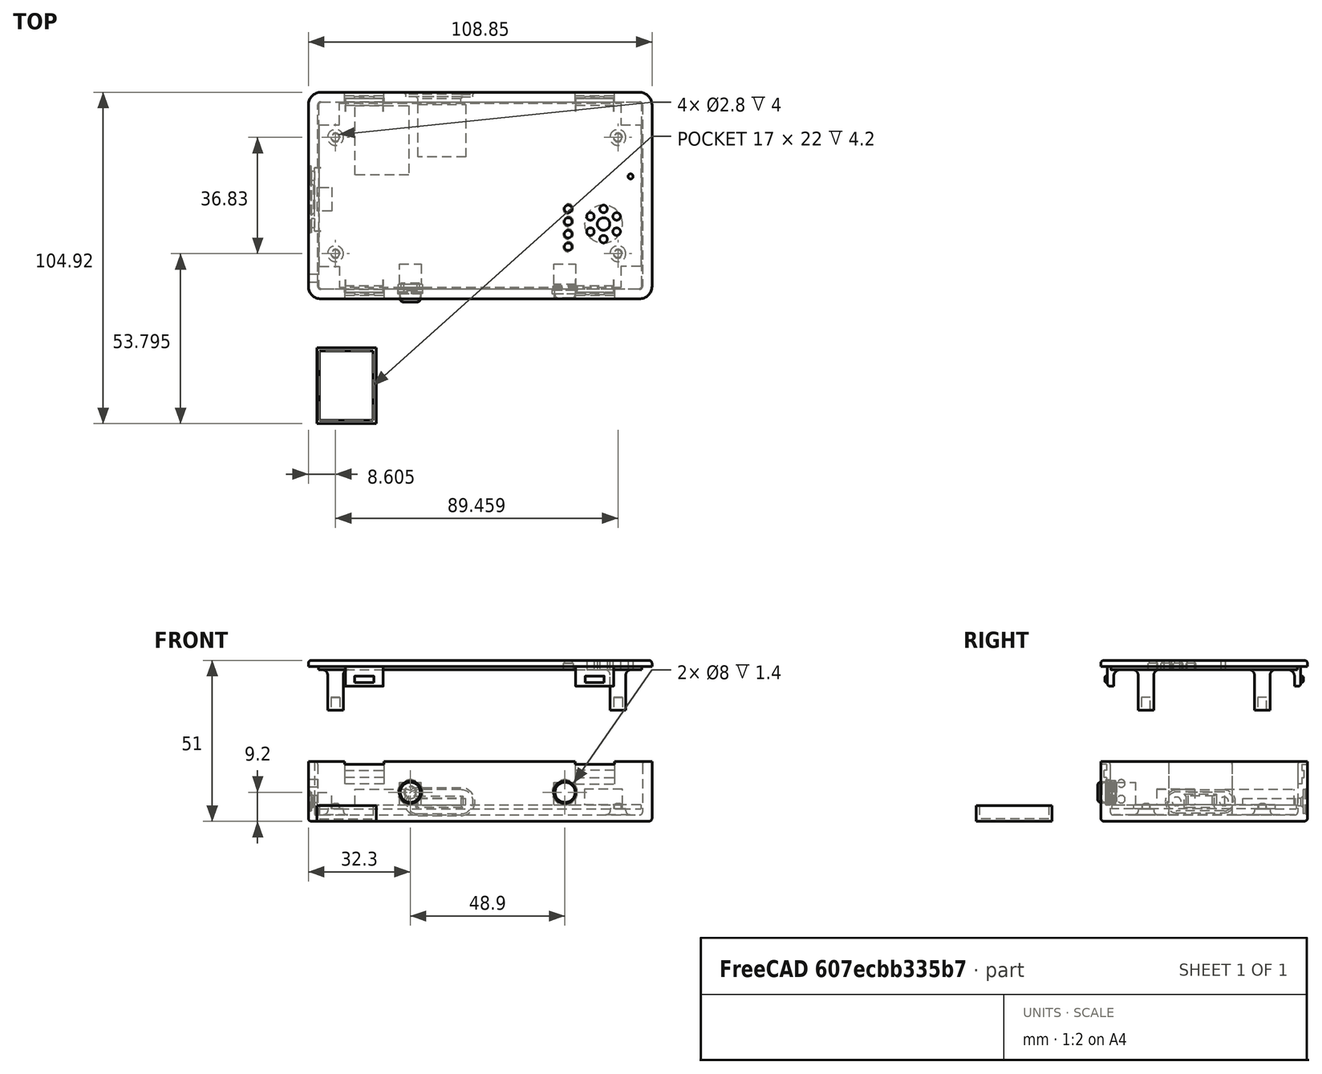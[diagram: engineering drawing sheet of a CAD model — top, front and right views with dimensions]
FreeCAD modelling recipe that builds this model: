
FCSTD DOCUMENT  (FreeCAD 0.17R13541 (Git))
Label: Variometer-Case-Rev2
License: All rights reserved
LicenseURL: http://en.wikipedia.org/wiki/All_rights_reserved
objects: Sketcher::SketchObject×48, PartDesign::Pad×24, PartDesign::Pocket×20, PartDesign::Fillet×18, PartDesign::Plane×12, PartDesign::Body×9, Mesh::Feature×5, PartDesign::ShapeBinder×4, PartDesign::Chamfer×3, Part::Feature×2
note: 184 computed .brp shape members not serialized (recipe doc carries the construction recipe); baked Part::Feature solids carry a one-line shape summary decoded from their .brp

FEATURE [Sketcher::SketchObject] Sketch  label="MasterSketch"
  MapMode = 5
  Support = -> [XY_Plane]
  sketch-geometry (27):
    g0: LineSegment StartX=0 StartY=58.42 StartZ=0 EndX=101.85 EndY=58.42 EndZ=0
    g1: LineSegment StartX=101.85 StartY=58.42 StartZ=0 EndX=101.85 EndY=0 EndZ=0
    g2: LineSegment StartX=101.85 StartY=0 StartZ=0 EndX=0 EndY=0 EndZ=0
    g3: LineSegment StartX=0 StartY=0 StartZ=0 EndX=0 EndY=58.42 EndZ=0
    g4: Circle CenterX=5.105 CenterY=10.795 CenterZ=0 NormalX=0 NormalY=0 NormalZ=1 AngleXU=0 Radius=2.5
    g5: Circle CenterX=5.105 CenterY=47.625 CenterZ=0 NormalX=0 NormalY=0 NormalZ=1 AngleXU=0 Radius=2.5
    g6: Circle CenterX=94.564 CenterY=10.795 CenterZ=0 NormalX=0 NormalY=0 NormalZ=1 AngleXU=0 Radius=2.5
    g7: Circle CenterX=94.564 CenterY=47.625 CenterZ=0 NormalX=0 NormalY=0 NormalZ=1 AngleXU=0 Radius=2.5
    g8: LineSegment StartX=28.3 StartY=53.4492 StartZ=0 EndX=28.3 EndY=63.3867 EndZ=0
    g9: LineSegment StartX=11.3 StartY=63.3867 StartZ=0 EndX=11.3 EndY=53.4492 EndZ=0
    g10: Circle CenterX=90 CenterY=20.2 CenterZ=0 NormalX=0 NormalY=0 NormalZ=1 AngleXU=0 Radius=7
    g11: Circle CenterX=78.8 CenterY=25 CenterZ=0 NormalX=0 NormalY=0 NormalZ=1 AngleXU=0 Radius=1
    g12: Circle CenterX=78.8 CenterY=21 CenterZ=0 NormalX=0 NormalY=0 NormalZ=1 AngleXU=0 Radius=1
    g13: Circle CenterX=78.8 CenterY=17 CenterZ=0 NormalX=0 NormalY=0 NormalZ=1 AngleXU=0 Radius=1
    g14: Circle CenterX=78.8 CenterY=13 CenterZ=0 NormalX=0 NormalY=0 NormalZ=1 AngleXU=0 Radius=1
    g15: Circle CenterX=98.56 CenterY=35.28 CenterZ=0 NormalX=0 NormalY=0 NormalZ=1 AngleXU=0 Radius=1
    g16: LineSegment StartX=46.46 StartY=63.8315 StartZ=0 EndX=46.46 EndY=53.6528 EndZ=0
    g17: LineSegment StartX=31.26 StartY=53.6528 StartZ=0 EndX=31.26 EndY=63.3799 EndZ=0
    g18: LineSegment StartX=164.118 StartY=59.2092 StartZ=0 EndX=164.118 EndY=40.2092 EndZ=0
    g19: LineSegment StartX=176.88 StartY=59.5541 StartZ=0 EndX=176.88 EndY=42.5541 EndZ=0
    g20: LineSegment StartX=-10.0374 StartY=20.5 StartZ=0 EndX=4.83678 EndY=20.5 EndZ=0
    g21: LineSegment StartX=-10.1738 StartY=28 StartZ=0 EndX=4.42739 EndY=28 EndZ=0
    g22: LineSegment StartX=-10.0374 StartY=35.5 StartZ=0 EndX=4.56386 EndY=35.5 EndZ=0
    g23: LineSegment StartX=28.8 StartY=5.89163 StartZ=0 EndX=28.8 EndY=-5.34826 EndZ=0
    g24: LineSegment StartX=77.7 StartY=5.89163 StartZ=0 EndX=77.7 EndY=-5.48472 EndZ=0
    g25: LineSegment StartX=8 StartY=6.13746 StartZ=0 EndX=8 EndY=-25.1864 EndZ=0
    g26: LineSegment StartX=81 StartY=5.59162 StartZ=0 EndX=81 EndY=-24.8827 EndZ=0
  constraints (67):
    c: Coincident(g0,g1)
    c: Coincident(g1,g2)
    c: Coincident(g2,g3)
    c: Coincident(g3,g0)
    c: Horizontal(g0)
    c: Horizontal(g2)
    c: Vertical(g1)
    c: Vertical(g3)
    c: DistanceX(g0,g0) = 101.85  'PCB_Width'
    c: DistanceY(g1,g1) = 58.42  'PCB_Height'
    c: Coincident(g2,g-1)
    c: DistanceX(g-1,g4) = 5.105
    c: Vertical(g4,g5)
    c: DistanceY(g-1,g4) = 10.795
    c: DistanceY(g-1,g5) = 47.625
    c: DistanceX(g-1,g6) = 94.564
    c: Vertical(g6,g7)
    c: Horizontal(g4,g6)
    c: Horizontal(g5,g7)
    c: Radius(g5) = 2.5  'PCBSupporterRadius'
    c: Equal(g5,g4)
    c: Equal(g5,g6)
    c: Equal(g5,g7)
    c: Vertical(g8)
    c: Vertical(g9)
    c: DistanceX(g-1,g10) = 90
    c: DistanceY(g-1,g10) = 20.2
    c: Radius(g10) = 7
    c: Vertical(g14,g13)
    c: Vertical(g13,g12)
    c: Vertical(g12,g11)
    c: DistanceX(g-1,g14) = 78.8
    c: Radius(g14) = 1
    c: Equal(g14,g13)
    c: Equal(g14,g12)
    c: Equal(g14,g11)
    c: DistanceY(g1,g14) = 13
    c: DistanceY(g1,g13) = 17
    c: DistanceY(g1,g12) = 21
    c: DistanceY(g1,g11) = 25
    c: DistanceX(g-1,g15) = 98.56
    c: DistanceY(g1,g15) = 35.28
    c: Vertical(g16)
    c: Vertical(g17)
    c: DistanceX(g-1,g17) = 31.26  'BT_X1'
    c: Radius(g15) = 1
    c: Vertical(g18)
    c: Vertical(g19)
    c: DistanceY(g18,g18) = 19  'totalHeight'
    c: DistanceY(g19,g19) = 17  'innerDepth'
    c: Horizontal(g20)
    c: Horizontal(g21)
    c: Horizontal(g22)
    c: DistanceY(g-1,g20) = 20.5  'ledGreeHeight'
    c: DistanceY(g-1,g21) = 28  'USBPos'
    c: DistanceY(g-1,g22) = 35.5  'RedLEDPos'
    c: Vertical(g23)
    c: Vertical(g24)
    c: DistanceX(g-1,g23) = 28.8
    c: DistanceX(g-1,g24) = 77.7
    c: DistanceX(g0,g16) = 46.46  'BT_X2'
    c: DistanceX(g0,g9) = 11.3  'IMU_X1'
    c: DistanceX(g0,g8) = 28.3  'IMU_X2'
    c: Vertical(g25)
    c: Vertical(g26)
    c: DistanceX(g-1,g25) = 8  'Locker_X1'
    c: DistanceX(g-1,g26) = 81  'Locker_X2'
FEATURE [PartDesign::Body] Body  label="MasterBlock"
  Group = -> [Sketch]
  Origin = -> Origin
FEATURE [PartDesign::ShapeBinder] ShapeBinder  label="BodyShapeBinder"
  Support = -> [Sketch]
FEATURE [Sketcher::SketchObject] Sketch001  label="Outer"
  ExternalGeometry = -> [ShapeBinder]
  MapMode = 5
  Support = -> [XY_Plane001]
  sketch-geometry (4):
    g0: LineSegment StartX=-3.5 StartY=61.92 StartZ=0 EndX=105.35 EndY=61.92 EndZ=0
    g1: LineSegment StartX=105.35 StartY=61.92 StartZ=0 EndX=105.35 EndY=-3.5 EndZ=0
    g2: LineSegment StartX=105.35 StartY=-3.5 StartZ=0 EndX=-3.5 EndY=-3.5 EndZ=0
    g3: LineSegment StartX=-3.5 StartY=-3.5 StartZ=0 EndX=-3.5 EndY=61.92 EndZ=0
  constraints (12):
    c: Coincident(g0,g1)
    c: Coincident(g1,g2)
    c: Coincident(g2,g3)
    c: Coincident(g3,g0)
    c: Horizontal(g0)
    c: Horizontal(g2)
    c: Vertical(g1)
    c: Vertical(g3)
    c: DistanceY(g2,g-1) = 3.5
    c: DistanceX(g2,g-1) = 3.5
    c: DistanceX(g-3,g0) = 3.5
    c: DistanceY(g-3,g0) = 3.5
FEATURE [PartDesign::Pad] Pad  label="OuterBlock"
  Length = 19
  Length2 = 100
  Profile = -> Sketch001
  Type = 0
  expr: Length = 19
FEATURE [PartDesign::Plane] DatumPlane  label="UpperPlane"
  MapMode = 45
  Placement = pos=(50.925,29.21,19) rot=(0,0,1;1.5708rad)
  Support = -> [Pad]
FEATURE [Sketcher::SketchObject] Sketch002  label="Inner"
  ExternalGeometry = -> [Pad]
  MapMode = 5
  Placement = pos=(50.925,29.21,19) rot=(0,0,1;1.5708rad)
  Support = -> [DatumPlane]
  sketch-geometry (4):
    g0: LineSegment StartX=-29.71 StartY=51.425 StartZ=0 EndX=29.71 EndY=51.425 EndZ=0
    g1: LineSegment StartX=29.71 StartY=51.425 StartZ=0 EndX=29.71 EndY=-51.425 EndZ=0
    g2: LineSegment StartX=29.71 StartY=-51.425 StartZ=0 EndX=-29.71 EndY=-51.425 EndZ=0
    g3: LineSegment StartX=-29.71 StartY=-51.425 StartZ=0 EndX=-29.71 EndY=51.425 EndZ=0
  constraints (12):
    c: Coincident(g0,g1)
    c: Coincident(g1,g2)
    c: Coincident(g2,g3)
    c: Coincident(g3,g0)
    c: Horizontal(g0)
    c: Horizontal(g2)
    c: Vertical(g1)
    c: Vertical(g3)
    c: DistanceY(g0,g-3) = 3
    c: DistanceX(g-3,g0) = 3
    c: DistanceX(g1,g-4) = 3
    c: DistanceY(g-4,g1) = 3
FEATURE [PartDesign::Pocket] Pocket  label="InnerBlock"
  BaseFeature = -> Pad
  Length = 17
  Length2 = 100
  Profile = -> Sketch002
  Type = 0
FEATURE [PartDesign::Plane] DatumPlane001  label="InnerBottom"
  MapMode = 5
  Placement = pos=(0,0,2) rot=(0,0,1;0rad)
  Support = -> [Pocket]
FEATURE [Sketcher::SketchObject] Sketch003  label="PCBSupport"
  ExternalGeometry = -> [ShapeBinder]
  MapMode = 5
  Placement = pos=(0,0,2) rot=(0,0,1;0rad)
  Support = -> [DatumPlane001]
  sketch-geometry (4):
    g0: Circle CenterX=5.105 CenterY=47.625 CenterZ=0 NormalX=0 NormalY=0 NormalZ=1 AngleXU=0 Radius=2.5
    g1: Circle CenterX=94.564 CenterY=47.625 CenterZ=0 NormalX=0 NormalY=0 NormalZ=1 AngleXU=0 Radius=2.5
    g2: Circle CenterX=94.564 CenterY=10.795 CenterZ=0 NormalX=0 NormalY=0 NormalZ=1 AngleXU=0 Radius=2.5
    g3: Circle CenterX=5.105 CenterY=10.795 CenterZ=0 NormalX=0 NormalY=0 NormalZ=1 AngleXU=0 Radius=2.5
  constraints (8):
    c: Coincident(g0,g-5)
    c: Coincident(g1,g-4)
    c: Coincident(g2,g-3)
    c: Coincident(g3,g-6)
    c: Equal(g3,g0)
    c: Equal(g0,g1)
    c: Equal(g1,g2)
    c: Radius(g3) = 2.5
FEATURE [PartDesign::Pad] Pad001  label="PCBSupportPad"
  BaseFeature = -> Pocket
  Length = 2
  Length2 = 100
  Profile = -> Sketch003
  Type = 0
FEATURE [PartDesign::Plane] DatumPlane002  label="PCBPlane"
  MapMode = 5
  Placement = pos=(0,0,4) rot=(0,0,1;0rad)
  Support = -> [Pad001]
FEATURE [Sketcher::SketchObject] Sketch004  label="PCBHole"
  ExternalGeometry = -> [Pad001]
  MapMode = 5
  Placement = pos=(0,0,4) rot=(0,0,1;0rad)
  Support = -> [DatumPlane002]
  sketch-geometry (4):
    g0: Circle CenterX=5.105 CenterY=47.625 CenterZ=0 NormalX=0 NormalY=0 NormalZ=1 AngleXU=0 Radius=1.2
    g1: Circle CenterX=94.564 CenterY=47.625 CenterZ=0 NormalX=0 NormalY=0 NormalZ=1 AngleXU=0 Radius=1.2
    g2: Circle CenterX=94.564 CenterY=10.795 CenterZ=0 NormalX=0 NormalY=0 NormalZ=1 AngleXU=0 Radius=1.2
    g3: Circle CenterX=5.105 CenterY=10.795 CenterZ=0 NormalX=0 NormalY=0 NormalZ=1 AngleXU=0 Radius=1.2
  constraints (8):
    c: Coincident(g0,g-6)
    c: Coincident(g1,g-3)
    c: Coincident(g3,g-5)
    c: Coincident(g-4,g2)
    c: Equal(g0,g3)
    c: Equal(g3,g2)
    c: Equal(g2,g1)
    c: Radius(g0) = 1.2
FEATURE [PartDesign::Pad] Pad002  label="PCBHolePocket"
  BaseFeature = -> Pad001
  Length = 1.6
  Length2 = 100
  Profile = -> Sketch004
  Type = 0
FEATURE [PartDesign::Plane] DatumPlane003  label="LeftSideInnerPlane"
  MapMode = 5
  Placement = pos=(0,58.92,0) rot=(1,0,0;1.5708rad)
  Support = -> [Pad002]
FEATURE [PartDesign::Plane] DatumPlane004  label="RightSideInnerPlane"
  MapMode = 5
  Placement = pos=(0,-0.5,0) rot=(0,0.707107,0.707107;3.14159rad)
  Support = -> [Pad002]
FEATURE [PartDesign::Plane] DatumPlane005  label="LowerSideInnerPlane"
  MapMode = 5
  Placement = pos=(-0.5,0,0) rot=(0.57735,0.57735,0.57735;2.0944rad)
  Support = -> [Pad002]
FEATURE [Sketcher::SketchObject] Sketch005  label="LeftSideInnerHoles"
  ExternalGeometry = -> [ShapeBinder,Pad002]
  MapMode = 5
  Placement = pos=(0,58.92,0) rot=(1,0,0;1.5708rad)
  Support = -> [DatumPlane003]
  sketch-geometry (12):
    g0: LineSegment StartX=8 StartY=19 StartZ=0 EndX=20.4 EndY=19 EndZ=0
    g1: LineSegment StartX=20.4 StartY=19 StartZ=0 EndX=20.4 EndY=18 EndZ=0
    g2: LineSegment StartX=20.4 StartY=18 StartZ=0 EndX=8 EndY=18 EndZ=0
    g3: LineSegment StartX=8 StartY=18 StartZ=0 EndX=8 EndY=19 EndZ=0
    g4: LineSegment StartX=81 StartY=19 StartZ=0 EndX=93.4 EndY=19 EndZ=0
    g5: LineSegment StartX=93.4 StartY=19 StartZ=0 EndX=93.4 EndY=18 EndZ=0
    g6: LineSegment StartX=93.4 StartY=18 StartZ=0 EndX=81 EndY=18 EndZ=0
    g7: LineSegment StartX=81 StartY=18 StartZ=0 EndX=81 EndY=19 EndZ=0
    g8: LineSegment StartX=31.26 StartY=7.4 StartZ=0 EndX=44.86 EndY=7.4 EndZ=0
    g9: LineSegment StartX=44.86 StartY=7.4 StartZ=0 EndX=44.86 EndY=5 EndZ=0
    g10: LineSegment StartX=44.86 StartY=5 StartZ=0 EndX=31.26 EndY=5 EndZ=0
    g11: LineSegment StartX=31.26 StartY=5 StartZ=0 EndX=31.26 EndY=7.4 EndZ=0
  constraints (36):
    c: Coincident(g0,g1)
    c: Coincident(g1,g2)
    c: Coincident(g2,g3)
    c: Coincident(g3,g0)
    c: Horizontal(g0)
    c: Horizontal(g2)
    c: Vertical(g1)
    c: Vertical(g3)
    c: Coincident(g4,g5)
    c: Coincident(g5,g6)
    c: Coincident(g6,g7)
    c: Coincident(g7,g4)
    c: Horizontal(g4)
    c: Horizontal(g6)
    c: Vertical(g5)
    c: Vertical(g7)
    c: Coincident(g8,g9)
    c: Coincident(g9,g10)
    c: Coincident(g10,g11)
    c: Coincident(g11,g8)
    c: Horizontal(g8)
    c: Horizontal(g10)
    c: Vertical(g9)
    c: Vertical(g11)
    c: Vertical(g-5,g2)
    c: Vertical(g-7,g6)
    c: Equal(g0,g4)
    c: Equal(g1,g5)
    c: Tangent(g0,g-6) = 1.5708
    c: PointOnObject(g4,g-6)
    c: Distance(g1) = 1
    c: Distance(g0) = 12.4
    c: Vertical(g-3,g10)
    c: DistanceY(g9,g9) = 2.4
    c: DistanceY(g-4,g9) = 5
    c: DistanceX(g8,g8) = 13.6
FEATURE [PartDesign::Pocket] Pocket001  label="LeftSideThroughHole"
  BaseFeature = -> Pad002
  Length = 5
  Length2 = 100
  Profile = -> Sketch005
  Type = 1
FEATURE [Sketcher::SketchObject] Sketch006  label="RightSideInnerHoles"
  ExternalGeometry = -> [ShapeBinder,Pocket001]
  MapMode = 5
  Placement = pos=(0,-0.5,0) rot=(0,0.707107,0.707107;3.14159rad)
  Support = -> [DatumPlane004]
  sketch-geometry (10):
    g0: LineSegment StartX=-93.4 StartY=19 StartZ=0 EndX=-81 EndY=19 EndZ=0
    g1: LineSegment StartX=-81 StartY=19 StartZ=0 EndX=-81 EndY=18 EndZ=0
    g2: LineSegment StartX=-81 StartY=18 StartZ=0 EndX=-93.4 EndY=18 EndZ=0
    g3: LineSegment StartX=-93.4 StartY=18 StartZ=0 EndX=-93.4 EndY=19 EndZ=0
    g4: LineSegment StartX=-20.4 StartY=19 StartZ=0 EndX=-8 EndY=19 EndZ=0
    g5: LineSegment StartX=-8 StartY=19 StartZ=0 EndX=-8 EndY=18 EndZ=0
    g6: LineSegment StartX=-8 StartY=18 StartZ=0 EndX=-20.4 EndY=18 EndZ=0
    g7: LineSegment StartX=-20.4 StartY=18 StartZ=0 EndX=-20.4 EndY=19 EndZ=0
    g8: Circle CenterX=-77.7 CenterY=9.2 CenterZ=0 NormalX=0 NormalY=0 NormalZ=1 AngleXU=0 Radius=3.4
    g9: Circle CenterX=-28.8 CenterY=9.2 CenterZ=0 NormalX=0 NormalY=0 NormalZ=1 AngleXU=0 Radius=3.4
  constraints (30):
    c: Coincident(g0,g1)
    c: Coincident(g1,g2)
    c: Coincident(g2,g3)
    c: Coincident(g3,g0)
    c: Horizontal(g0)
    c: Horizontal(g2)
    c: Vertical(g1)
    c: Vertical(g3)
    c: Coincident(g4,g5)
    c: Coincident(g5,g6)
    c: Coincident(g6,g7)
    c: Coincident(g7,g4)
    c: Horizontal(g4)
    c: Horizontal(g6)
    c: Vertical(g5)
    c: Vertical(g7)
    c: PointOnObject(g0,g-7)
    c: PointOnObject(g4,g-7)
    c: Vertical(g-6,g1)
    c: Vertical(g-5,g5)
    c: Equal(g7,g3)
    c: DistanceY(g1,g1) = 1
    c: DistanceX(g0,g0) = 12.4
    c: Equal(g8,g9)
    c: Radius(g9) = 3.4
    c: Equal(g4,g0)
    c: Vertical(g-3,g8)
    c: Vertical(g-4,g9)
    c: Horizontal(g8,g9)
    c: DistanceY(g-4,g9) = 9.2
FEATURE [PartDesign::Pocket] Pocket002  label="RightSideThroughHole"
  BaseFeature = -> Pocket001
  Length = 5
  Length2 = 100
  Profile = -> Sketch006
  Type = 1
FEATURE [Sketcher::SketchObject] Sketch007  label="FrontSideInnderHoles"
  ExternalGeometry = -> [ShapeBinder]
  MapMode = 5
  Placement = pos=(-0.5,0,0) rot=(0.57735,0.57735,0.57735;2.0944rad)
  Support = -> [DatumPlane005]
  sketch-geometry (8):
    g0: Circle CenterX=20.5 CenterY=6.3 CenterZ=0 NormalX=0 NormalY=0 NormalZ=1 AngleXU=0 Radius=1.4
    g1: Circle CenterX=35.5 CenterY=6.3 CenterZ=0 NormalX=0 NormalY=0 NormalZ=1 AngleXU=0 Radius=1.4
    g2: LineSegment StartX=23.5 StartY=8 StartZ=0 EndX=32.5 EndY=8 EndZ=0
    g3: LineSegment StartX=32.5 StartY=8 StartZ=0 EndX=32.5 EndY=4.5 EndZ=0
    g4: LineSegment StartX=32.5 StartY=4.5 StartZ=0 EndX=23.5 EndY=4.5 EndZ=0
    g5: LineSegment StartX=23.5 StartY=4.5 StartZ=0 EndX=23.5 EndY=8 EndZ=0
    g6: LineSegment [constr] StartX=28 StartY=0 StartZ=0 EndX=28 EndY=8 EndZ=0
    g7: LineSegment [constr] StartX=23.5 StartY=4.5 StartZ=0 EndX=35.5 EndY=4.5 EndZ=0
  constraints (24):
    c: Coincident(g2,g3)
    c: Coincident(g3,g4)
    c: Coincident(g4,g5)
    c: Coincident(g5,g2)
    c: Horizontal(g2)
    c: Horizontal(g4)
    c: Vertical(g3)
    c: Vertical(g5)
    c: Coincident(g6,g-3)
    c: Vertical(g6)
    c: Horizontal(g7)
    c: DistanceY(g-4,g7) = 4.5
    c: Symmetric(g2,g2,g6)
    c: DistanceX(g2,g2) = 9
    c: Vertical(g1,g-4)
    c: Vertical(g-5,g0)
    c: Horizontal(g0,g1)
    c: Equal(g0,g1)
    c: Radius(g0) = 1.4
    c: DistanceY(g3,g3) = 3.5
    c: DistanceY(g4,g0) = 1.8
    c: PointOnObject(g6,g2)
    c: Coincident(g7,g4)
    c: Vertical(g7,g1)
FEATURE [PartDesign::Pocket] Pocket003  label="FrontSideThroughHole"
  BaseFeature = -> Pocket002
  Length = 5
  Length2 = 100
  Profile = -> Sketch007
  Type = 1
FEATURE [PartDesign::Plane] DatumPlane006  label="RightSideOuterPlane"
  MapMode = 5
  Placement = pos=(0,61.92,0) rot=(0,0.707107,0.707107;3.14159rad)
  Support = -> [Pocket003]
FEATURE [PartDesign::Plane] DatumPlane007  label="LowerSideOuterPlane"
  MapMode = 5
  Placement = pos=(-3.5,0,0) rot=(0.57735,-0.57735,-0.57735;2.0944rad)
  Support = -> [Pocket003]
FEATURE [Sketcher::SketchObject] Sketch008  label="LockerHole"
  ExternalGeometry = -> [Pocket003]
  MapMode = 5
  Placement = pos=(50.925,29.21,19) rot=(0,0,1;1.5708rad)
  Support = -> [DatumPlane]
  sketch-geometry (16):
    g0: LineSegment StartX=-30.91 StartY=42.925 StartZ=0 EndX=-29.71 EndY=42.925 EndZ=0
    g1: LineSegment StartX=-29.71 StartY=42.925 StartZ=0 EndX=-29.71 EndY=30.525 EndZ=0
    g2: LineSegment StartX=-29.71 StartY=30.525 StartZ=0 EndX=-30.91 EndY=30.525 EndZ=0
    g3: LineSegment StartX=-30.91 StartY=30.525 StartZ=0 EndX=-30.91 EndY=42.925 EndZ=0
    g4: LineSegment StartX=30.91 StartY=42.925 StartZ=0 EndX=29.71 EndY=42.925 EndZ=0
    g5: LineSegment StartX=30.91 StartY=42.925 StartZ=0 EndX=30.91 EndY=30.525 EndZ=0
    g6: LineSegment StartX=30.91 StartY=30.525 StartZ=0 EndX=29.71 EndY=30.525 EndZ=0
    g7: LineSegment StartX=29.71 StartY=30.525 StartZ=0 EndX=29.71 EndY=42.925 EndZ=0
    g8: LineSegment StartX=29.71 StartY=-30.075 StartZ=0 EndX=30.91 EndY=-30.075 EndZ=0
    g9: LineSegment StartX=29.71 StartY=-30.075 StartZ=0 EndX=29.71 EndY=-42.475 EndZ=0
    g10: LineSegment StartX=29.71 StartY=-42.475 StartZ=0 EndX=30.91 EndY=-42.475 EndZ=0
    g11: LineSegment StartX=30.91 StartY=-42.475 StartZ=0 EndX=30.91 EndY=-30.075 EndZ=0
    g12: LineSegment StartX=-29.71 StartY=-30.075 StartZ=0 EndX=-30.91 EndY=-30.075 EndZ=0
    g13: LineSegment StartX=-30.91 StartY=-30.075 StartZ=0 EndX=-30.91 EndY=-42.475 EndZ=0
    g14: LineSegment StartX=-30.91 StartY=-42.475 StartZ=0 EndX=-29.71 EndY=-42.475 EndZ=0
    g15: LineSegment StartX=-29.71 StartY=-42.475 StartZ=0 EndX=-29.71 EndY=-30.075 EndZ=0
  constraints (44):
    c: Coincident(g0,g1)
    c: Coincident(g1,g2)
    c: Coincident(g2,g3)
    c: Horizontal(g0)
    c: Horizontal(g2)
    c: Vertical(g1)
    c: Vertical(g3)
    c: Coincident(g5,g6)
    c: Coincident(g6,g7)
    c: Horizontal(g4)
    c: Horizontal(g6)
    c: Vertical(g5)
    c: Vertical(g7)
    c: Coincident(g9,g10)
    c: Coincident(g10,g11)
    c: Horizontal(g8)
    c: Horizontal(g10)
    c: Vertical(g9)
    c: Vertical(g11)
    c: Coincident(g12,g13)
    c: Coincident(g13,g14)
    c: Coincident(g14,g15)
    c: Coincident(g15,g12)
    c: Horizontal(g12)
    c: Horizontal(g14)
    c: Vertical(g13)
    c: Vertical(g15)
    c: Equal(g12,g8)
    c: Equal(g8,g2)
    c: Equal(g2,g6)
    c: DistanceX(g2,g2) = 1.2
    c: Coincident(g7,g4)
    c: Coincident(g5,g4)
    c: Coincident(g9,g8)
    c: Coincident(g8,g11)
    c: Coincident(g3,g0)
    c: Coincident(g0,g-3)
    c: Coincident(g-3,g1)
    c: Coincident(g4,g-4)
    c: Coincident(g6,g-4)
    c: Coincident(g9,g-5)
    c: Coincident(g8,g-5)
    c: Coincident(g14,g-6)
    c: Coincident(g-6,g12)
FEATURE [PartDesign::Pocket] Pocket004  label="LockerInnerPocker"
  BaseFeature = -> Pocket003
  Length = 7.2
  Length2 = 100
  Profile = -> Sketch008
  Type = 0
FEATURE [Sketcher::SketchObject] Sketch009  label="LeftSideLockingHole"
  ExternalGeometry = -> [Pocket004]
  MapMode = 5
  Placement = pos=(0,58.92,0) rot=(1,0,0;1.5708rad)
  Support = -> [DatumPlane003]
  sketch-geometry (8):
    g0: LineSegment StartX=8 StartY=16.2 StartZ=0 EndX=20.4 EndY=16.2 EndZ=0
    g1: LineSegment StartX=20.4 StartY=16.2 StartZ=0 EndX=20.4 EndY=13.8 EndZ=0
    g2: LineSegment StartX=20.4 StartY=13.8 StartZ=0 EndX=8 EndY=13.8 EndZ=0
    g3: LineSegment StartX=8 StartY=13.8 StartZ=0 EndX=8 EndY=16.2 EndZ=0
    g4: LineSegment StartX=81 StartY=16.2 StartZ=0 EndX=93.4 EndY=16.2 EndZ=0
    g5: LineSegment StartX=93.4 StartY=16.2 StartZ=0 EndX=93.4 EndY=13.8 EndZ=0
    g6: LineSegment StartX=93.4 StartY=13.8 StartZ=0 EndX=81 EndY=13.8 EndZ=0
    g7: LineSegment StartX=81 StartY=13.8 StartZ=0 EndX=81 EndY=16.2 EndZ=0
  constraints (24):
    c: Coincident(g0,g1)
    c: Coincident(g1,g2)
    c: Coincident(g2,g3)
    c: Coincident(g3,g0)
    c: Horizontal(g0)
    c: Horizontal(g2)
    c: Vertical(g1)
    c: Vertical(g3)
    c: Coincident(g4,g5)
    c: Coincident(g5,g6)
    c: Coincident(g6,g7)
    c: Coincident(g7,g4)
    c: Horizontal(g4)
    c: Horizontal(g6)
    c: Vertical(g5)
    c: Vertical(g7)
    c: Vertical(g-3,g0)
    c: Vertical(g-3,g0)
    c: Vertical(g-4,g4)
    c: Vertical(g-4,g4)
    c: Equal(g1,g7)
    c: DistanceY(g0,g-3) = 1.8
    c: DistanceY(g1,g0) = 2.4
    c: Horizontal(g4,g0)
FEATURE [PartDesign::Pocket] Pocket005  label="LeftSideLockingHolePocket"
  BaseFeature = -> Pocket004
  Length = 2
  Length2 = 100
  Profile = -> Sketch009
  Type = 0
FEATURE [Sketcher::SketchObject] Sketch010  label="RightSideLockingHole"
  ExternalGeometry = -> [Pocket005]
  MapMode = 5
  Placement = pos=(0,-0.5,0) rot=(0,0.707107,0.707107;3.14159rad)
  Support = -> [DatumPlane004]
  sketch-geometry (8):
    g0: LineSegment StartX=-93.4 StartY=16.2 StartZ=0 EndX=-81 EndY=16.2 EndZ=0
    g1: LineSegment StartX=-81 StartY=16.2 StartZ=0 EndX=-81 EndY=13.8 EndZ=0
    g2: LineSegment StartX=-81 StartY=13.8 StartZ=0 EndX=-93.4 EndY=13.8 EndZ=0
    g3: LineSegment StartX=-93.4 StartY=13.8 StartZ=0 EndX=-93.4 EndY=16.2 EndZ=0
    g4: LineSegment StartX=-20.4 StartY=16.2 StartZ=0 EndX=-8 EndY=16.2 EndZ=0
    g5: LineSegment StartX=-8 StartY=16.2 StartZ=0 EndX=-8 EndY=13.8 EndZ=0
    g6: LineSegment StartX=-8 StartY=13.8 StartZ=0 EndX=-20.4 EndY=13.8 EndZ=0
    g7: LineSegment StartX=-20.4 StartY=13.8 StartZ=0 EndX=-20.4 EndY=16.2 EndZ=0
  constraints (24):
    c: Coincident(g0,g1)
    c: Coincident(g1,g2)
    c: Coincident(g2,g3)
    c: Coincident(g3,g0)
    c: Horizontal(g0)
    c: Horizontal(g2)
    c: Vertical(g1)
    c: Vertical(g3)
    c: Coincident(g4,g5)
    c: Coincident(g5,g6)
    c: Coincident(g6,g7)
    c: Coincident(g7,g4)
    c: Horizontal(g4)
    c: Horizontal(g6)
    c: Vertical(g5)
    c: Vertical(g7)
    c: Horizontal(g0,g4)
    c: Vertical(g0,g-3)
    c: Vertical(g-3,g0)
    c: Vertical(g-4,g4)
    c: Vertical(g-4,g4)
    c: DistanceY(g0,g-3) = 1.8
    c: Distance(g1) = 2.4
    c: Equal(g1,g7)
FEATURE [PartDesign::Pocket] Pocket006  label="RightSideLockingHolePocket"
  BaseFeature = -> Pocket005
  Length = 2
  Length2 = 100
  Profile = -> Sketch010
  Type = 0
FEATURE [Sketcher::SketchObject] Sketch011  label="KeyOuter"
  ExternalGeometry = -> [Pocket006]
  MapMode = 5
  Placement = pos=(0,-0.5,0) rot=(0,0.707107,0.707107;3.14159rad)
  Support = -> [DatumPlane004]
  sketch-geometry (2):
    g0: Circle CenterX=-77.7 CenterY=9.2 CenterZ=0 NormalX=0 NormalY=0 NormalZ=1 AngleXU=0 Radius=4
    g1: Circle CenterX=-28.8 CenterY=9.2 CenterZ=0 NormalX=0 NormalY=0 NormalZ=1 AngleXU=0 Radius=4
  constraints (4):
    c: Coincident(g0,g-4)
    c: Coincident(g1,g-3)
    c: Equal(g1,g0)
    c: Radius(g1) = 4
FEATURE [PartDesign::Pocket] Pocket007  label="KeyOuterPocket"
  BaseFeature = -> Pocket006
  Length = 1.4
  Length2 = 100
  Profile = -> Sketch011
  Type = 0
FEATURE [PartDesign::ShapeBinder] ShapeBinder001  label="CoverShapeBinder"
  Support = -> [Sketch]
FEATURE [PartDesign::Plane] DatumPlane008  label="CoverBasePlane"
  AttachmentOffset = pos=(0,0,49) rot=(0,0,1;0rad)
  MapMode = 45
  Placement = pos=(50.925,29.21,49) rot=(0,0,1;1.5708rad)
  Support = -> [ShapeBinder001]
FEATURE [Sketcher::SketchObject] Sketch012  label="CoverOuter"
  ExternalGeometry = -> [ShapeBinder001]
  MapMode = 5
  Placement = pos=(50.925,29.21,49) rot=(0,0,1;1.5708rad)
  Support = -> [DatumPlane008]
  sketch-geometry (4):
    g0: LineSegment StartX=-32.71 StartY=54.425 StartZ=0 EndX=32.71 EndY=54.425 EndZ=0
    g1: LineSegment StartX=32.71 StartY=54.425 StartZ=0 EndX=32.71 EndY=-54.425 EndZ=0
    g2: LineSegment StartX=32.71 StartY=-54.425 StartZ=0 EndX=-32.71 EndY=-54.425 EndZ=0
    g3: LineSegment StartX=-32.71 StartY=-54.425 StartZ=0 EndX=-32.71 EndY=54.425 EndZ=0
  constraints (12):
    c: Coincident(g0,g1)
    c: Coincident(g1,g2)
    c: Coincident(g2,g3)
    c: Coincident(g3,g0)
    c: Horizontal(g0)
    c: Horizontal(g2)
    c: Vertical(g1)
    c: Vertical(g3)
    c: DistanceY(g-3,g0) = 3.5
    c: DistanceX(g0,g-3) = 3.5
    c: DistanceY(g1,g-5) = 3.5
    c: DistanceX(g-5,g1) = 3.5
FEATURE [PartDesign::Pad] Pad003  label="CoverOuterBlock"
  Length = 2
  Length2 = 100
  Placement = pos=(50.925,29.21,49) rot=(0,0,1;1.5708rad)
  Profile = -> Sketch012
  Type = 0
FEATURE [Sketcher::SketchObject] Sketch017  label="CoverInner"
  ExternalGeometry = -> [Pad003]
  MapMode = 5
  Placement = pos=(50.925,29.21,49) rot=(0.707107,0.707107,0;3.14159rad)
  Support = -> [Pad003]
  sketch-geometry (4):
    g0: LineSegment StartX=-29.51 StartY=51.225 StartZ=0 EndX=29.51 EndY=51.225 EndZ=0
    g1: LineSegment StartX=29.51 StartY=51.225 StartZ=0 EndX=29.51 EndY=-51.225 EndZ=0
    g2: LineSegment StartX=29.51 StartY=-51.225 StartZ=0 EndX=-29.51 EndY=-51.225 EndZ=0
    g3: LineSegment StartX=-29.51 StartY=-51.225 StartZ=0 EndX=-29.51 EndY=51.225 EndZ=0
  constraints (12):
    c: Coincident(g0,g1)
    c: Coincident(g1,g2)
    c: Coincident(g2,g3)
    c: Coincident(g3,g0)
    c: Horizontal(g0)
    c: Horizontal(g2)
    c: Vertical(g1)
    c: Vertical(g3)
    c: DistanceX(g-4,g0) = 3.2
    c: DistanceY(g0,g-4) = 3.2
    c: DistanceY(g-3,g1) = 3.2
    c: DistanceX(g1,g-3) = 3.2
FEATURE [PartDesign::Pad] Pad004  label="ConerInnerBlock"
  BaseFeature = -> Pad003
  Length = 1
  Length2 = 100
  Placement = pos=(50.925,29.21,49) rot=(0,0,1;1.5708rad)
  Profile = -> Sketch017
  Type = 0
FEATURE [PartDesign::Plane] DatumPlane009  label="CoverInnerPlane"
  MapMode = 5
  Placement = pos=(50.925,29.21,48) rot=(0.707107,0.707107,0;3.14159rad)
  Support = -> [Pad004]
FEATURE [Sketcher::SketchObject] Sketch018  label="CoverPCBSupport"
  ExternalGeometry = -> [ShapeBinder001]
  MapMode = 5
  Placement = pos=(50.925,29.21,48) rot=(0.707107,0.707107,0;3.14159rad)
  Support = -> [DatumPlane009]
  sketch-geometry (4):
    g0: Circle CenterX=-18.415 CenterY=43.639 CenterZ=0 NormalX=0 NormalY=0 NormalZ=1 AngleXU=0 Radius=2.5
    g1: Circle CenterX=18.415 CenterY=43.639 CenterZ=0 NormalX=0 NormalY=0 NormalZ=1 AngleXU=0 Radius=2.5
    g2: Circle CenterX=-18.415 CenterY=-45.82 CenterZ=0 NormalX=0 NormalY=0 NormalZ=1 AngleXU=0 Radius=2.5
    g3: Circle CenterX=18.415 CenterY=-45.82 CenterZ=0 NormalX=0 NormalY=0 NormalZ=1 AngleXU=0 Radius=2.5
  constraints (8):
    c: Coincident(g0,g-3)
    c: Coincident(g1,g-4)
    c: Coincident(g2,g-6)
    c: Coincident(g3,g-5)
    c: Equal(g2,g3)
    c: Equal(g3,g0)
    c: Equal(g0,g1)
    c: Radius(g1) = 2.5
FEATURE [PartDesign::Pad] Pad005  label="CoverPCBSupportPad"
  BaseFeature = -> Pad004
  Length = 12.8
  Length2 = 100
  Placement = pos=(50.925,29.21,49) rot=(0,0,1;1.5708rad)
  Profile = -> Sketch018
  Type = 0
FEATURE [PartDesign::Plane] DatumPlane010  label="CoverPCBPlane"
  MapMode = 5
  Placement = pos=(50.925,29.21,35.2) rot=(0.707107,0.707107,0;3.14159rad)
  Support = -> [Pad005]
FEATURE [Sketcher::SketchObject] Sketch019  label="CoverPCBHole"
  ExternalGeometry = -> [ShapeBinder001]
  MapMode = 5
  Placement = pos=(50.925,29.21,35.2) rot=(0.707107,0.707107,0;3.14159rad)
  Support = -> [DatumPlane010]
  sketch-geometry (4):
    g0: Circle CenterX=-18.415 CenterY=-45.82 CenterZ=0 NormalX=0 NormalY=0 NormalZ=1 AngleXU=0 Radius=1.4
    g1: Circle CenterX=18.415 CenterY=-45.82 CenterZ=0 NormalX=0 NormalY=0 NormalZ=1 AngleXU=0 Radius=1.4
    g2: Circle CenterX=-18.415 CenterY=43.639 CenterZ=0 NormalX=0 NormalY=0 NormalZ=1 AngleXU=0 Radius=1.4
    g3: Circle CenterX=18.415 CenterY=43.639 CenterZ=0 NormalX=0 NormalY=0 NormalZ=1 AngleXU=0 Radius=1.4
  constraints (8):
    c: Coincident(g0,g-5)
    c: Coincident(g1,g-6)
    c: Coincident(g2,g-3)
    c: Coincident(g3,g-4)
    c: Equal(g2,g3)
    c: Equal(g3,g0)
    c: Equal(g0,g1)
    c: Radius(g3) = 1.4
FEATURE [PartDesign::Pocket] Pocket008  label="CoverPCBHolePocket"
  BaseFeature = -> Pad005
  Length = 4
  Length2 = 100
  Placement = pos=(50.925,29.21,49) rot=(0,0,1;1.5708rad)
  Profile = -> Sketch019
  Type = 0
FEATURE [Sketcher::SketchObject] Sketch020  label="CoverHoles"
  ExternalGeometry = -> [ShapeBinder001]
  MapMode = 5
  Placement = pos=(50.925,29.21,48) rot=(0.707107,0.707107,0;3.14159rad)
  Support = -> [DatumPlane009]
  sketch-geometry (19):
    g0: Circle CenterX=-16.21 CenterY=27.875 CenterZ=0 NormalX=0 NormalY=0 NormalZ=1 AngleXU=0 Radius=1.2
    g1: Circle CenterX=-12.21 CenterY=27.875 CenterZ=0 NormalX=0 NormalY=0 NormalZ=1 AngleXU=0 Radius=1.2
    g2: Circle CenterX=-8.21 CenterY=27.875 CenterZ=0 NormalX=0 NormalY=0 NormalZ=1 AngleXU=0 Radius=1.2
    g3: Circle CenterX=-4.21 CenterY=27.875 CenterZ=0 NormalX=0 NormalY=0 NormalZ=1 AngleXU=0 Radius=1.2
    g4: Circle CenterX=-9.01 CenterY=39.075 CenterZ=0 NormalX=0 NormalY=0 NormalZ=1 AngleXU=0 Radius=2
    g5: Circle CenterX=6.07 CenterY=47.635 CenterZ=0 NormalX=0 NormalY=0 NormalZ=1 AngleXU=0 Radius=0.8
    g6: LineSegment [constr] StartX=-6.61 StartY=34.9181 StartZ=0 EndX=-4.21 EndY=39.075 EndZ=0
    g7: LineSegment [constr] StartX=-4.21 StartY=39.075 StartZ=0 EndX=-6.61 EndY=43.2319 EndZ=0
    g8: LineSegment [constr] StartX=-6.61 StartY=43.2319 StartZ=0 EndX=-11.41 EndY=43.2319 EndZ=0
    g9: LineSegment [constr] StartX=-11.41 StartY=43.2319 StartZ=0 EndX=-13.81 EndY=39.075 EndZ=0
    g10: LineSegment [constr] StartX=-13.81 StartY=39.075 StartZ=0 EndX=-11.41 EndY=34.9181 EndZ=0
    g11: LineSegment [constr] StartX=-11.41 StartY=34.9181 StartZ=0 EndX=-6.61 EndY=34.9181 EndZ=0
    g12: Circle [constr] CenterX=-9.01 CenterY=39.075 CenterZ=0 NormalX=0 NormalY=0 NormalZ=1 AngleXU=0 Radius=4.8
    g13: Circle CenterX=-6.61 CenterY=34.9181 CenterZ=0 NormalX=0 NormalY=0 NormalZ=1 AngleXU=0 Radius=1.2
    g14: Circle CenterX=-11.41 CenterY=34.9181 CenterZ=0 NormalX=0 NormalY=0 NormalZ=1 AngleXU=0 Radius=1.2
    g15: Circle CenterX=-13.81 CenterY=39.075 CenterZ=0 NormalX=0 NormalY=0 NormalZ=1 AngleXU=0 Radius=1.2
    g16: Circle CenterX=-11.41 CenterY=43.2319 CenterZ=0 NormalX=0 NormalY=0 NormalZ=1 AngleXU=0 Radius=1.2
    g17: Circle CenterX=-6.61 CenterY=43.2319 CenterZ=0 NormalX=0 NormalY=0 NormalZ=1 AngleXU=0 Radius=1.2
    g18: Circle CenterX=-4.21 CenterY=39.075 CenterZ=0 NormalX=0 NormalY=0 NormalZ=1 AngleXU=0 Radius=1.2
  constraints (40):
    c: Coincident(g0,g-4)
    c: Coincident(g1,g-5)
    c: Coincident(g2,g-6)
    c: Coincident(g3,g-7)
    c: Coincident(g4,g-3)
    c: Coincident(g5,g-8)
    c: Coincident(g6,g7)
    c: Coincident(g7,g8)
    c: Coincident(g8,g9)
    c: Coincident(g9,g10)
    c: Coincident(g10,g11)
    c: Coincident(g11,g6)
    c: Equal(g6, g7-g11) x5
    c: PointOnObject(g6,g12)
    c: PointOnObject(g7,g12)
    c: PointOnObject(g8,g12)
    c: PointOnObject(g9,g12)
    c: PointOnObject(g10,g12)
    c: PointOnObject(g11,g12)
    c: Coincident(g12,g4)
    c: Coincident(g13,g6)
    c: Coincident(g14,g10)
    c: Coincident(g15,g9)
    c: Coincident(g16,g8)
    c: Coincident(g17,g7)
    c: Coincident(g18,g6)
    c: Horizontal(g4,g6)
    c: Equal(g15,g16)
    c: Equal(g16,g17)
    c: Equal(g17,g18)
    c: Equal(g18,g13)
    c: Equal(g13,g14)
    c: Equal(g0,g1)
    c: Equal(g1,g2)
    c: Equal(g2,g3)
    c: Radius(g3) = 1.2
    c: Radius(g5) = 0.8
    c: Radius(g4) = 2
    c: Radius(g13) = 1.2
    c: Distance(g7) = 4.8
FEATURE [PartDesign::Pocket] Pocket009  label="CoverThroughHoles"
  BaseFeature = -> Pocket008
  Length = 5
  Length2 = 100
  Placement = pos=(50.925,29.21,49) rot=(0,0,1;1.5708rad)
  Profile = -> Sketch020
  Type = 1
FEATURE [PartDesign::Plane] DatumPlane011  label="CoverBelowPlane"
  MapMode = 5
  Placement = pos=(50.925,29.21,49) rot=(0.707107,0.707107,0;3.14159rad)
  Support = -> [Pocket009]
FEATURE [Sketcher::SketchObject] Sketch021  label="CoverLockingBar"
  ExternalGeometry = -> [ShapeBinder001]
  MapMode = 5
  Placement = pos=(50.925,29.21,49) rot=(0.707107,0.707107,0;3.14159rad)
  Support = -> [DatumPlane011]
  sketch-geometry (16):
    g0: LineSegment StartX=-30.61 StartY=-30.725 StartZ=0 EndX=-28.61 EndY=-30.725 EndZ=0
    g1: LineSegment StartX=-28.61 StartY=-30.725 StartZ=0 EndX=-28.61 EndY=-42.725 EndZ=0
    g2: LineSegment StartX=-28.61 StartY=-42.725 StartZ=0 EndX=-30.61 EndY=-42.725 EndZ=0
    g3: LineSegment StartX=-30.61 StartY=-42.725 StartZ=0 EndX=-30.61 EndY=-30.725 EndZ=0
    g4: LineSegment StartX=-30.61 StartY=42.275 StartZ=0 EndX=-28.61 EndY=42.275 EndZ=0
    g5: LineSegment StartX=-28.61 StartY=42.275 StartZ=0 EndX=-28.61 EndY=30.275 EndZ=0
    g6: LineSegment StartX=-28.61 StartY=30.275 StartZ=0 EndX=-30.61 EndY=30.275 EndZ=0
    g7: LineSegment StartX=-30.61 StartY=30.275 StartZ=0 EndX=-30.61 EndY=42.275 EndZ=0
    g8: LineSegment StartX=28.61 StartY=42.275 StartZ=0 EndX=30.61 EndY=42.275 EndZ=0
    g9: LineSegment StartX=30.61 StartY=42.275 StartZ=0 EndX=30.61 EndY=30.275 EndZ=0
    g10: LineSegment StartX=30.61 StartY=30.275 StartZ=0 EndX=28.61 EndY=30.275 EndZ=0
    g11: LineSegment StartX=28.61 StartY=30.275 StartZ=0 EndX=28.61 EndY=42.275 EndZ=0
    g12: LineSegment StartX=28.61 StartY=-30.725 StartZ=0 EndX=30.61 EndY=-30.725 EndZ=0
    g13: LineSegment StartX=30.61 StartY=-30.725 StartZ=0 EndX=30.61 EndY=-42.725 EndZ=0
    g14: LineSegment StartX=30.61 StartY=-42.725 StartZ=0 EndX=28.61 EndY=-42.725 EndZ=0
    g15: LineSegment StartX=28.61 StartY=-42.725 StartZ=0 EndX=28.61 EndY=-30.725 EndZ=0
  constraints (48):
    c: Coincident(g0,g1)
    c: Coincident(g1,g2)
    c: Coincident(g2,g3)
    c: Coincident(g3,g0)
    c: Horizontal(g0)
    c: Horizontal(g2)
    c: Vertical(g1)
    c: Vertical(g3)
    c: Coincident(g4,g5)
    c: Coincident(g5,g6)
    c: Coincident(g6,g7)
    c: Coincident(g7,g4)
    c: Horizontal(g4)
    c: Horizontal(g6)
    c: Vertical(g5)
    c: Vertical(g7)
    c: Coincident(g8,g9)
    c: Coincident(g9,g10)
    c: Coincident(g10,g11)
    c: Coincident(g11,g8)
    c: Horizontal(g8)
    c: Horizontal(g10)
    c: Vertical(g9)
    c: Vertical(g11)
    c: Coincident(g12,g13)
    c: Coincident(g13,g14)
    c: Coincident(g14,g15)
    c: Coincident(g15,g12)
    c: Horizontal(g12)
    c: Horizontal(g14)
    c: Vertical(g13)
    c: Vertical(g15)
    c: Equal(g3,g7)
    c: Equal(g7,g11)
    c: Equal(g11,g15)
    c: Equal(g4,g0)
    c: Equal(g0,g12)
    c: Equal(g12,g8)
    c: DistanceX(g0,g0) = 2
    c: DistanceY(g1,g1) = 12
    c: DistanceY(g-5,g5) = 0.2
    c: Horizontal(g5,g10)
    c: DistanceY(g-5,g1) = 0.2
    c: Horizontal(g1,g14)
    c: DistanceX(g-5,g5) = 0.6
    c: DistanceX(g-5,g1) = 0.6
    c: DistanceX(g14,g-6) = 0.6
    c: DistanceX(g10,g-6) = 0.6
FEATURE [PartDesign::Pad] Pad006  label="CoverLockingBarPad"
  BaseFeature = -> Pocket009
  Length = 6.2
  Length2 = 100
  Placement = pos=(50.925,29.21,49) rot=(0,0,1;1.5708rad)
  Profile = -> Sketch021
  Type = 0
FEATURE [Sketcher::SketchObject] Sketch022  label="LeftLockingLatch"
  ExternalGeometry = -> [Pad006]
  MapMode = 5
  Placement = pos=(50.925,59.82,49) rot=(0,0.707107,0.707107;3.14159rad)
  Support = -> [Pad006]
  sketch-geometry (8):
    g0: LineSegment StartX=-39.275 StartY=-3 StartZ=0 EndX=-33.275 EndY=-3 EndZ=0
    g1: LineSegment StartX=-33.275 StartY=-3 StartZ=0 EndX=-33.275 EndY=-5 EndZ=0
    g2: LineSegment StartX=-33.275 StartY=-5 StartZ=0 EndX=-39.275 EndY=-5 EndZ=0
    g3: LineSegment StartX=-39.275 StartY=-5 StartZ=0 EndX=-39.275 EndY=-3 EndZ=0
    g4: LineSegment StartX=33.725 StartY=-3 StartZ=0 EndX=39.725 EndY=-3 EndZ=0
    g5: LineSegment StartX=39.725 StartY=-3 StartZ=0 EndX=39.725 EndY=-5 EndZ=0
    g6: LineSegment StartX=39.725 StartY=-5 StartZ=0 EndX=33.725 EndY=-5 EndZ=0
    g7: LineSegment StartX=33.725 StartY=-5 StartZ=0 EndX=33.725 EndY=-3 EndZ=0
  constraints (24):
    c: Coincident(g0,g1)
    c: Coincident(g1,g2)
    c: Coincident(g2,g3)
    c: Coincident(g3,g0)
    c: Horizontal(g0)
    c: Horizontal(g2)
    c: Vertical(g1)
    c: Vertical(g3)
    c: Coincident(g4,g5)
    c: Coincident(g5,g6)
    c: Coincident(g6,g7)
    c: Coincident(g7,g4)
    c: Horizontal(g4)
    c: Horizontal(g6)
    c: Vertical(g5)
    c: Vertical(g7)
    c: Horizontal(g0,g4)
    c: Horizontal(g1,g6)
    c: Distance(g1) = 2
    c: DistanceY(g0,g-4) = 3
    c: DistanceX(g-3,g0) = 3
    c: DistanceX(g0,g-4) = 3
    c: DistanceX(g-5,g4) = 3
    c: DistanceX(g4,g-6) = 3
FEATURE [PartDesign::Pad] Pad007  label="LeftLockingLatchPad"
  BaseFeature = -> Pad006
  Length = 0.8
  Length2 = 100
  Placement = pos=(50.925,29.21,49) rot=(0,0,1;1.5708rad)
  Profile = -> Sketch022
  Type = 0
FEATURE [Sketcher::SketchObject] Sketch023  label="RightLockingLatch"
  ExternalGeometry = -> [Pad007]
  MapMode = 5
  Placement = pos=(50.925,-1.4,49) rot=(1,0,0;1.5708rad)
  Support = -> [Pad007]
  sketch-geometry (8):
    g0: LineSegment StartX=-39.725 StartY=-3 StartZ=0 EndX=-33.725 EndY=-3 EndZ=0
    g1: LineSegment StartX=-33.725 StartY=-3 StartZ=0 EndX=-33.725 EndY=-5 EndZ=0
    g2: LineSegment StartX=-33.725 StartY=-5 StartZ=0 EndX=-39.725 EndY=-5 EndZ=0
    g3: LineSegment StartX=-39.725 StartY=-5 StartZ=0 EndX=-39.725 EndY=-3 EndZ=0
    g4: LineSegment StartX=33.275 StartY=-3 StartZ=0 EndX=39.275 EndY=-3 EndZ=0
    g5: LineSegment StartX=39.275 StartY=-3 StartZ=0 EndX=39.275 EndY=-5 EndZ=0
    g6: LineSegment StartX=39.275 StartY=-5 StartZ=0 EndX=33.275 EndY=-5 EndZ=0
    g7: LineSegment StartX=33.275 StartY=-5 StartZ=0 EndX=33.275 EndY=-3 EndZ=0
  constraints (24):
    c: Coincident(g0,g1)
    c: Coincident(g1,g2)
    c: Coincident(g2,g3)
    c: Coincident(g3,g0)
    c: Horizontal(g0)
    c: Horizontal(g2)
    c: Vertical(g1)
    c: Vertical(g3)
    c: Coincident(g4,g5)
    c: Coincident(g5,g6)
    c: Coincident(g6,g7)
    c: Coincident(g7,g4)
    c: Horizontal(g4)
    c: Horizontal(g6)
    c: Vertical(g5)
    c: Vertical(g7)
    c: Horizontal(g0,g4)
    c: Distance(g1) = 2
    c: DistanceY(g0,g-4) = 3
    c: Equal(g7,g1)
    c: DistanceX(g-3,g0) = 3
    c: DistanceX(g0,g-4) = 3
    c: DistanceX(g-5,g4) = 3
    c: DistanceX(g4,g-6) = 3
FEATURE [PartDesign::Pad] Pad008  label="RightLockingLatchPad"
  BaseFeature = -> Pad007
  Length = 0.8
  Length2 = 100
  Placement = pos=(50.925,29.21,49) rot=(0,0,1;1.5708rad)
  Profile = -> Sketch023
  Type = 0
FEATURE [Sketcher::SketchObject] Sketch024  label="CarHoleGuide"
  ExternalGeometry = -> [Pocket007]
  MapMode = 5
  Placement = pos=(0,61.92,0) rot=(0,0.707107,0.707107;3.14159rad)
  Support = -> [Pocket007]
  sketch-geometry (4):
    g0: ArcOfCircle CenterX=-44.86 CenterY=6.2 CenterZ=0 NormalX=0 NormalY=0 NormalZ=1 AngleXU=0 Radius=3.8 StartAngle=1.5708 EndAngle=4.71239
    g1: ArcOfCircle CenterX=-31.26 CenterY=6.2 CenterZ=0 NormalX=0 NormalY=0 NormalZ=1 AngleXU=0 Radius=3.8 StartAngle=4.71239 EndAngle=7.85398
    g2: LineSegment StartX=-44.86 StartY=2.4 StartZ=0 EndX=-31.26 EndY=2.4 EndZ=0
    g3: LineSegment StartX=-44.86 StartY=10 StartZ=0 EndX=-31.26 EndY=10 EndZ=0
  constraints (9):
    c: Tangent(g0,g3) = 1.5708
    c: Tangent(g0,g2) = -1.5708
    c: Tangent(g2,g1) = -1.5708
    c: Tangent(g3,g1) = 1.5708
    c: Horizontal(g2)
    c: Equal(g0,g1)
    c: Symmetric(g-4,g-3,g0)
    c: Symmetric(g-3,g-4,g1)
    c: DistanceY(g-3,g0) = 2.6
FEATURE [PartDesign::Pocket] Pocket010  label="CardHoleGuidePocket"
  BaseFeature = -> Pocket007
  Length = 1.4
  Length2 = 100
  Profile = -> Sketch024
  Type = 0
FEATURE [Sketcher::SketchObject] Sketch025  label="FrontGuide"
  ExternalGeometry = -> [Pocket010]
  MapMode = 5
  Placement = pos=(-3.5,0,0) rot=(0.57735,-0.57735,-0.57735;2.0944rad)
  Support = -> [Pocket010]
  sketch-geometry (4):
    g0: ArcOfCircle CenterX=-35.5 CenterY=6.3 CenterZ=0 NormalX=0 NormalY=0 NormalZ=1 AngleXU=0 Radius=3 StartAngle=1.5708 EndAngle=4.71239
    g1: ArcOfCircle CenterX=-20.5 CenterY=6.3 CenterZ=0 NormalX=0 NormalY=0 NormalZ=1 AngleXU=0 Radius=3 StartAngle=4.71239 EndAngle=7.85398
    g2: LineSegment StartX=-35.5 StartY=3.3 StartZ=0 EndX=-20.5 EndY=3.3 EndZ=0
    g3: LineSegment StartX=-35.5 StartY=9.3 StartZ=0 EndX=-20.5 EndY=9.3 EndZ=0
  constraints (9):
    c: Tangent(g0,g3) = 1.5708
    c: Tangent(g0,g2) = -1.5708
    c: Tangent(g2,g1) = -1.5708
    c: Tangent(g3,g1) = 1.5708
    c: Horizontal(g2)
    c: Equal(g0,g1)
    c: DistanceY(g0,g0) = 3
    c: Coincident(g0,g-3)
    c: Vertical(g1,g-4)
FEATURE [PartDesign::Pocket] Pocket011  label="FrontGuidePocket"
  BaseFeature = -> Pocket010
  Length = 1
  Length2 = 100
  Profile = -> Sketch025
  Type = 0
FEATURE [PartDesign::ShapeBinder] ShapeBinder002  label="ButtonShapeBinder"
  Support = -> [Sketch]
FEATURE [Sketcher::SketchObject] Sketch026  label="ButtonBase"
  ExternalGeometry = -> [ShapeBinder002]
  MapMode = 5
  Placement = pos=(0,0,0) rot=(1,0,0;1.5708rad)
  Support = -> [XZ_Plane003]
  sketch-geometry (1):
    g0: Circle CenterX=28.8 CenterY=9.2 CenterZ=0 NormalX=0 NormalY=0 NormalZ=1 AngleXU=0 Radius=3.8
  constraints (3):
    c: Radius(g0) = 3.8
    c: Vertical(g0,g-3)
    c: DistanceY(g-3,g0) = 9.2
FEATURE [PartDesign::Pad] Pad009  label="ButtonBasePad"
  Length = 3
  Length2 = 100
  Placement = pos=(0,0,0) rot=(1,0,0;1.5708rad)
  Profile = -> Sketch026
  Type = 0
FEATURE [Sketcher::SketchObject] Sketch027  label="ButtonBody"
  ExternalGeometry = -> [Pad009]
  MapMode = 5
  Placement = pos=(0,-3,0) rot=(1,0,0;1.5708rad)
  Support = -> [Pad009]
  sketch-geometry (1):
    g0: Circle CenterX=28.8 CenterY=9.2 CenterZ=0 NormalX=0 NormalY=0 NormalZ=1 AngleXU=0 Radius=3.2
  constraints (2):
    c: Coincident(g0,g-3)
    c: Radius(g0) = 3.2
FEATURE [PartDesign::Pad] Pad010  label="ButtonBodyPad"
  BaseFeature = -> Pad009
  Length = 2.6
  Length2 = 100
  Placement = pos=(0,0,0) rot=(1,0,0;1.5708rad)
  Profile = -> Sketch027
  Type = 0
FEATURE [PartDesign::Fillet] Fillet  label="FilletButtonEdge"
  Base = -> Pad010 [Edge6]
  BaseFeature = -> Pad010
  Placement = pos=(0,0,0) rot=(1,0,0;1.5708rad)
  Radius = 1
FEATURE [Sketcher::SketchObject] Sketch028  label="LowerSideSunken"
  ExternalGeometry = -> [ShapeBinder,Pocket011]
  MapMode = 5
  Placement = pos=(50.925,29.21,19) rot=(0,0,1;1.5708rad)
  Support = -> [DatumPlane]
  sketch-geometry (4):
    g0: LineSegment StartX=-11.21 StartY=52.425 StartZ=0 EndX=8.79 EndY=52.425 EndZ=0
    g1: LineSegment StartX=8.79 StartY=52.425 StartZ=0 EndX=8.79 EndY=51.425 EndZ=0
    g2: LineSegment StartX=8.79 StartY=51.425 StartZ=0 EndX=-11.21 EndY=51.425 EndZ=0
    g3: LineSegment StartX=-11.21 StartY=51.425 StartZ=0 EndX=-11.21 EndY=52.425 EndZ=0
  constraints (12):
    c: Coincident(g0,g1)
    c: Coincident(g1,g2)
    c: Coincident(g2,g3)
    c: Coincident(g3,g0)
    c: Horizontal(g0)
    c: Horizontal(g2)
    c: Vertical(g1)
    c: Vertical(g3)
    c: Symmetric(g0,g0,g-3)
    c: PointOnObject(g1,g-4)
    c: DistanceY(g3,g3) = 1
    c: DistanceX(g0,g0) = 20
FEATURE [PartDesign::Pocket] Pocket012  label="LowerSideSunkenPocket"
  BaseFeature = -> Pocket011
  Length = 17
  Length2 = 100
  Profile = -> Sketch028
  Type = 0
FEATURE [PartDesign::Fillet] Fillet001  label="FilletOuter"
  Base = -> Pocket012 [Edge20,Edge2,Edge26,Edge3]
  BaseFeature = -> Pocket012
  Radius = 4
FEATURE [PartDesign::Fillet] Fillet002  label="FilletInner"
  Base = -> Fillet001 [Edge94,Edge97,Edge138,Edge134]
  BaseFeature = -> Fillet001
  Radius = 1
FEATURE [PartDesign::Fillet] Fillet003  label="FilletBottom"
  Base = -> Fillet002 [Edge94]
  BaseFeature = -> Fillet002
  Radius = 1
FEATURE [PartDesign::Chamfer] Chamfer  label="ChamferLower"
  Base = -> Fillet003 [Edge84,Edge253,Edge247,Edge251,Edge249]
  BaseFeature = -> Fillet003
  Size = 0.6
FEATURE [PartDesign::Chamfer] Chamfer001  label="ChamferCard"
  Base = -> Chamfer [Edge119,Edge253,Edge252,Edge249,Edge247]
  BaseFeature = -> Chamfer
  Size = 0.6
FEATURE [PartDesign::Chamfer] Chamfer002  label="ChamferButtonHole"
  Base = -> Chamfer001 [Edge157,Edge158]
  BaseFeature = -> Chamfer001
  Size = 0.1
FEATURE [PartDesign::Fillet] Fillet004  label="FilletCoverOuter"
  Base = -> Pad008 [Edge2,Edge8,Edge5,Edge1]
  BaseFeature = -> Pad008
  Placement = pos=(50.925,29.21,49) rot=(0,0,1;1.5708rad)
  Radius = 4
FEATURE [PartDesign::Fillet] Fillet005  label="FilletCoverInner"
  Base = -> Fillet004 [Edge57,Edge59,Edge94,Edge93]
  BaseFeature = -> Fillet004
  Placement = pos=(50.925,29.21,49) rot=(0,0,1;1.5708rad)
  Radius = 1
FEATURE [PartDesign::Fillet] Fillet006  label="FilletCoverTop"
  Base = -> Fillet005 [Edge123]
  BaseFeature = -> Fillet005
  Placement = pos=(50.925,29.21,49) rot=(0,0,1;1.5708rad)
  Radius = 1
FEATURE [PartDesign::Fillet] Fillet007  label="FilletLockingBar"
  Base = -> Fillet006 [Edge118,Edge86,Edge91,Edge123]
  BaseFeature = -> Fillet006
  Placement = pos=(50.925,29.21,49) rot=(0,0,1;1.5708rad)
  Radius = 0.8
FEATURE [PartDesign::Fillet] Fillet008  label="FilletLockingLatchBottom"
  Base = -> Fillet007 [Edge229,Edge95,Edge237,Edge221]
  BaseFeature = -> Fillet007
  Placement = pos=(50.925,29.21,49) rot=(0,0,1;1.5708rad)
  Radius = 0.4
FEATURE [PartDesign::Fillet] Fillet009  label="FilletLockingLatchTop"
  Base = -> Fillet008 [Edge237,Edge215,Edge18,Edge227]
  BaseFeature = -> Fillet008
  Placement = pos=(50.925,29.21,49) rot=(0,0,1;1.5708rad)
  Radius = 0.4
FEATURE [Sketcher::SketchObject] Sketch029  label="ButtonHole"
  ExternalGeometry = -> [Fillet]
  MapMode = 5
  Placement = pos=(0,0,0) rot=(-1,0,0;1.5708rad)
  Support = -> [Fillet]
  sketch-geometry (1):
    g0: Circle CenterX=28.8 CenterY=-9.2 CenterZ=0 NormalX=0 NormalY=0 NormalZ=1 AngleXU=0 Radius=2
  constraints (2):
    c: Coincident(g0,g-3)
    c: Radius(g0) = 2
FEATURE [PartDesign::Pocket] Pocket013  label="ButtonHolePocket"
  BaseFeature = -> Fillet
  Length = 1
  Length2 = 100
  Placement = pos=(0,0,0) rot=(1,0,0;1.5708rad)
  Profile = -> Sketch029
  Type = 0
FEATURE [PartDesign::Body] Body003  label="ButtonBlock"
  Group = -> [ShapeBinder002,Sketch026,Pad009,Sketch027,Pad010,Fillet,Sketch029,Pocket013]
  Origin = -> Origin003
  Placement = pos=(0,1.1,0) rot=(0,0,1;0rad)
  Tip = -> Pocket013
FEATURE [PartDesign::Fillet] Fillet010  label="FilletSupport"
  Base = -> Chamfer002 [Edge204,Edge203,Edge206,Edge205]
  BaseFeature = -> Chamfer002
  Radius = 1.4
FEATURE [PartDesign::Fillet] Fillet011  label="FilletCoverSupport"
  Base = -> Fillet009 [Edge103,Edge104,Edge101,Edge98]
  BaseFeature = -> Fillet009
  Placement = pos=(50.925,29.21,49) rot=(0,0,1;1.5708rad)
  Radius = 1.6
FEATURE [PartDesign::Fillet] Fillet012  label="FilletCoverLockingBar"
  Base = -> Fillet011 [Edge6,Edge14,Edge21,Edge13]
  BaseFeature = -> Fillet011
  Placement = pos=(50.925,29.21,49) rot=(0,0,1;1.5708rad)
  Radius = 2
FEATURE [PartDesign::Fillet] Fillet013  label="FilletInnerBottom"
  Base = -> Fillet010 [Edge5]
  BaseFeature = -> Fillet010
  Radius = 1
FEATURE [PartDesign::Fillet] Fillet014  label="FilletInnerUpper"
  Base = -> Fillet013 [Edge102,Edge91,Edge55,Edge126,Edge46]
  BaseFeature = -> Fillet013
  Radius = 1
FEATURE [Sketcher::SketchObject] Sketch030  label="LEDHole"
  ExternalGeometry = -> [ShapeBinder001]
  MapMode = 5
  Placement = pos=(50.925,29.21,48) rot=(0.707107,0.707107,0;3.14159rad)
  sketch-geometry (4):
    g0: Circle CenterX=-16.21 CenterY=27.875 CenterZ=0 NormalX=0 NormalY=0 NormalZ=1 AngleXU=0 Radius=1.6
    g1: Circle CenterX=-12.21 CenterY=27.875 CenterZ=0 NormalX=0 NormalY=0 NormalZ=1 AngleXU=0 Radius=1.6
    g2: Circle CenterX=-8.21 CenterY=27.875 CenterZ=0 NormalX=0 NormalY=0 NormalZ=1 AngleXU=0 Radius=1.6
    g3: Circle CenterX=-4.21 CenterY=27.875 CenterZ=0 NormalX=0 NormalY=0 NormalZ=1 AngleXU=0 Radius=1.6
  constraints (8):
    c: Coincident(g0,g-3)
    c: Coincident(g1,g-4)
    c: Coincident(g2,g-5)
    c: Coincident(g3,g-6)
    c: Equal(g0,g1)
    c: Equal(g1,g2)
    c: Equal(g2,g3)
    c: Radius(g0) = 1.6
FEATURE [PartDesign::Pocket] Pocket014  label="LEDHolePoket"
  BaseFeature = -> Fillet012
  Length = 2
  Length2 = 100
  Placement = pos=(50.925,29.21,49) rot=(0,0,1;1.5708rad)
  Profile = -> Sketch030
  Type = 0
FEATURE [PartDesign::Fillet] Fillet016  label="FilletPCBHole"
  Base = -> Fillet014 [Edge437,Edge431,Edge433,Edge435]
  BaseFeature = -> Fillet014
  Radius = 0.6
FEATURE [Sketcher::SketchObject] Sketch031
  MapMode = 5
  Placement = pos=(-3.5,0,0) rot=(0.57735,-0.57735,-0.57735;2.0944rad)
  Support = -> [Fillet016]
  sketch-geometry (2):
    g0: Circle CenterX=-8 CenterY=7 CenterZ=0 NormalX=0 NormalY=0 NormalZ=1 AngleXU=0 Radius=1.2
    g1: Circle CenterX=-3 CenterY=7 CenterZ=0 NormalX=0 NormalY=0 NormalZ=1 AngleXU=0 Radius=1.2
  constraints (6):
    c: Radius(g1) = 1.2
    c: Equal(g1,g0)
    c: Horizontal(g1,g0)
    c: DistanceX(g0,g1) = 5
    c: DistanceX(g1,g-1) = 3
    c: DistanceY(g-1,g1) = 7
FEATURE [Part::Feature] Face  label="Paraglider1"
  shape: bbox 34.23 x 12.19 x 2e-07 mm, 1 faces, 0 solids (baked)
FEATURE [Part::Feature] Face001  label="Paraglider2"
  shape: bbox 30.14 x 17.68 x 2e-07 mm, 1 faces, 0 solids (baked)
FEATURE [Sketcher::SketchObject] Sketch032
  MapMode = 5
  Support = -> [Face001]
FEATURE [PartDesign::Body] Body002  label="CoverBlock"
  Group = -> [ShapeBinder001,DatumPlane008,Sketch012,Pad003,Sketch017,Pad004,DatumPlane009,Sketch018,Pad005,DatumPlane010,Sketch019,Pocket008,Sketch020,Pocket009,DatumPlane011,Sketch021,Pad006,Sketch022,Pad007,Sketch023,Pad008,Fillet004,Fillet005,Fillet006,Fillet007,Fillet008,Fillet009,Fillet011,Fillet012,Sketch030,Pocket014,Sketch032]
  Origin = -> Origin002
  Tip = -> Pocket014
FEATURE [PartDesign::ShapeBinder] ShapeBinder003
  Support = -> [Sketch]
FEATURE [Sketcher::SketchObject] Sketch033  label="PCB"
  ExternalGeometry = -> [ShapeBinder003]
  MapMode = 5
  Support = -> [XY_Plane004]
  sketch-geometry (4):
    g0: LineSegment StartX=0 StartY=58.42 StartZ=0 EndX=101.85 EndY=58.42 EndZ=0
    g1: LineSegment StartX=101.85 StartY=58.42 StartZ=0 EndX=101.85 EndY=0 EndZ=0
    g2: LineSegment StartX=101.85 StartY=0 StartZ=0 EndX=0 EndY=0 EndZ=0
    g3: LineSegment StartX=0 StartY=0 StartZ=0 EndX=0 EndY=58.42 EndZ=0
  constraints (10):
    c: Coincident(g0,g1)
    c: Coincident(g1,g2)
    c: Coincident(g2,g3)
    c: Coincident(g3,g0)
    c: Horizontal(g0)
    c: Horizontal(g2)
    c: Vertical(g1)
    c: Vertical(g3)
    c: Coincident(g2,g-1)
    c: Coincident(g0,g-3)
FEATURE [PartDesign::Pad] Pad011  label="PCBPad"
  Length = 1.2
  Length2 = 100
  Profile = -> Sketch033
  Type = 0
FEATURE [Sketcher::SketchObject] Sketch034  label="Corner"
  ExternalGeometry = -> [Pad011]
  MapMode = 5
  Placement = pos=(0,0,1.2) rot=(0,0,1;0rad)
  Support = -> [Pad011]
  sketch-geometry (16):
    g0: LineSegment StartX=0 StartY=58.42 StartZ=0 EndX=6.366 EndY=58.42 EndZ=0
    g1: LineSegment StartX=6.366 StartY=58.42 StartZ=0 EndX=6.366 EndY=51.609 EndZ=0
    g2: LineSegment StartX=6.366 StartY=51.609 StartZ=0 EndX=0 EndY=51.609 EndZ=0
    g3: LineSegment StartX=0 StartY=51.609 StartZ=0 EndX=0 EndY=58.42 EndZ=0
    g4: LineSegment StartX=95.484 StartY=58.42 StartZ=0 EndX=101.85 EndY=58.42 EndZ=0
    g5: LineSegment StartX=101.85 StartY=58.42 StartZ=0 EndX=101.85 EndY=51.609 EndZ=0
    g6: LineSegment StartX=101.85 StartY=51.609 StartZ=0 EndX=95.484 EndY=51.609 EndZ=0
    g7: LineSegment StartX=95.484 StartY=51.609 StartZ=0 EndX=95.484 EndY=58.42 EndZ=0
    g8: LineSegment StartX=101.85 StartY=0 StartZ=0 EndX=95.484 EndY=0 EndZ=0
    g9: LineSegment StartX=95.484 StartY=0 StartZ=0 EndX=95.484 EndY=6.811 EndZ=0
    g10: LineSegment StartX=95.484 StartY=6.811 StartZ=0 EndX=101.85 EndY=6.811 EndZ=0
    g11: LineSegment StartX=101.85 StartY=6.811 StartZ=0 EndX=101.85 EndY=0 EndZ=0
    g12: LineSegment StartX=0 StartY=0 StartZ=0 EndX=6.366 EndY=0 EndZ=0
    g13: LineSegment StartX=6.366 StartY=0 StartZ=0 EndX=6.366 EndY=6.811 EndZ=0
    g14: LineSegment StartX=6.366 StartY=6.811 StartZ=0 EndX=0 EndY=6.811 EndZ=0
    g15: LineSegment StartX=0 StartY=6.811 StartZ=0 EndX=0 EndY=0 EndZ=0
  constraints (44):
    c: Coincident(g0,g1)
    c: Coincident(g1,g2)
    c: Coincident(g2,g3)
    c: Coincident(g3,g0)
    c: Horizontal(g0)
    c: Horizontal(g2)
    c: Vertical(g1)
    c: Vertical(g3)
    c: Coincident(g4,g5)
    c: Coincident(g5,g6)
    c: Coincident(g6,g7)
    c: Coincident(g7,g4)
    c: Horizontal(g4)
    c: Horizontal(g6)
    c: Vertical(g5)
    c: Vertical(g7)
    c: Coincident(g8,g9)
    c: Coincident(g9,g10)
    c: Coincident(g10,g11)
    c: Coincident(g11,g8)
    c: Horizontal(g8)
    c: Horizontal(g10)
    c: Vertical(g9)
    c: Vertical(g11)
    c: Coincident(g12,g13)
    c: Coincident(g13,g14)
    c: Coincident(g14,g15)
    c: Coincident(g15,g12)
    c: Horizontal(g12)
    c: Horizontal(g14)
    c: Vertical(g13)
    c: Vertical(g15)
    c: Equal(g0,g4)
    c: Equal(g4,g10)
    c: Equal(g10,g14)
    c: Equal(g1,g5)
    c: Equal(g5,g11)
    c: Equal(g11,g13)
    c: DistanceX(g0,g0) = 6.366
    c: DistanceY(g3,g3) = 6.811
    c: Coincident(g0,g-3)
    c: Coincident(g4,g-3)
    c: Coincident(g8,g-4)
    c: Coincident(g12,g-1)
FEATURE [PartDesign::Pocket] Pocket017  label="CornerPocket"
  BaseFeature = -> Pad011
  Length = 5
  Length2 = 100
  Profile = -> Sketch034
  Type = 1
FEATURE [Sketcher::SketchObject] Sketch035  label="Hole"
  ExternalGeometry = -> [ShapeBinder003]
  MapMode = 5
  Placement = pos=(0,0,1.2) rot=(0,0,1;0rad)
  Support = -> [Pocket017]
  sketch-geometry (4):
    g0: Circle CenterX=5.105 CenterY=47.625 CenterZ=0 NormalX=0 NormalY=0 NormalZ=1 AngleXU=0 Radius=1.25
    g1: Circle CenterX=94.564 CenterY=47.625 CenterZ=0 NormalX=0 NormalY=0 NormalZ=1 AngleXU=0 Radius=1.25
    g2: Circle CenterX=94.564 CenterY=10.795 CenterZ=0 NormalX=0 NormalY=0 NormalZ=1 AngleXU=0 Radius=1.25
    g3: Circle CenterX=5.105 CenterY=10.795 CenterZ=0 NormalX=0 NormalY=0 NormalZ=1 AngleXU=0 Radius=1.25
  constraints (8):
    c: Coincident(g0,g-3)
    c: Coincident(g1,g-5)
    c: Coincident(g2,g-6)
    c: Coincident(g3,g-4)
    c: Radius(g0) = 1.25
    c: Equal(g0,g1)
    c: Equal(g0,g2)
    c: Equal(g0,g3)
FEATURE [PartDesign::Pocket] Pocket018  label="HolePocket"
  BaseFeature = -> Pocket017
  Length = 5
  Length2 = 100
  Profile = -> Sketch035
  Type = 1
FEATURE [Sketcher::SketchObject] Sketch036  label="Buzzer"
  MapMode = 5
  Placement = pos=(0,0,1.2) rot=(0,0,1;0rad)
  Support = -> [Pocket018]
  sketch-geometry (1):
    g0: Circle CenterX=90 CenterY=20.2 CenterZ=0 NormalX=0 NormalY=0 NormalZ=1 AngleXU=0 Radius=6
  constraints (3):
    c: DistanceX(g-1,g0) = 90
    c: DistanceY(g-1,g0) = 20.2
    c: Radius(g0) = 6
FEATURE [Sketcher::SketchObject] Sketch037  label="Button"
  ExternalGeometry = -> [ShapeBinder003]
  MapMode = 5
  Placement = pos=(0,0,1.2) rot=(0,0,1;0rad)
  Support = -> [Pocket018]
  sketch-geometry (8):
    g0: LineSegment StartX=25.38 StartY=7.53 StartZ=0 EndX=32.22 EndY=7.53 EndZ=0
    g1: LineSegment StartX=32.22 StartY=7.53 StartZ=0 EndX=32.22 EndY=1.13 EndZ=0
    g2: LineSegment StartX=32.22 StartY=1.13 StartZ=0 EndX=25.38 EndY=1.13 EndZ=0
    g3: LineSegment StartX=25.38 StartY=1.13 StartZ=0 EndX=25.38 EndY=7.53 EndZ=0
    g4: LineSegment StartX=74.23 StartY=7.53 StartZ=0 EndX=81.17 EndY=7.53 EndZ=0
    g5: LineSegment StartX=81.17 StartY=7.53 StartZ=0 EndX=81.17 EndY=1.13 EndZ=0
    g6: LineSegment StartX=81.17 StartY=1.13 StartZ=0 EndX=74.23 EndY=1.13 EndZ=0
    g7: LineSegment StartX=74.23 StartY=1.13 StartZ=0 EndX=74.23 EndY=7.53 EndZ=0
  constraints (24):
    c: Coincident(g0,g1)
    c: Coincident(g1,g2)
    c: Coincident(g2,g3)
    c: Coincident(g3,g0)
    c: Horizontal(g0)
    c: Horizontal(g2)
    c: Vertical(g1)
    c: Vertical(g3)
    c: Symmetric(g2,g1,g-3)
    c: DistanceX(g-1,g2) = 25.38
    c: DistanceY(g-1,g2) = 1.13
    c: DistanceY(g-1,g0) = 7.53
    c: Coincident(g4,g5)
    c: Coincident(g5,g6)
    c: Coincident(g6,g7)
    c: Coincident(g7,g4)
    c: Horizontal(g4)
    c: Horizontal(g6)
    c: Vertical(g5)
    c: Vertical(g7)
    c: Symmetric(g6,g5,g-4)
    c: DistanceX(g-1,g6) = 74.23
    c: Horizontal(g4,g0)
    c: Horizontal(g6,g1)
FEATURE [Sketcher::SketchObject] Sketch038  label="SDCard"
  MapMode = 5
  Placement = pos=(0,0,1.2) rot=(0,0,1;0rad)
  Support = -> [Pocket018]
  sketch-geometry (4):
    g0: LineSegment StartX=31.25 StartY=58.09 StartZ=0 EndX=46.41 EndY=58.09 EndZ=0
    g1: LineSegment StartX=46.41 StartY=58.09 StartZ=0 EndX=46.41 EndY=41.48 EndZ=0
    g2: LineSegment StartX=46.41 StartY=41.48 StartZ=0 EndX=31.25 EndY=41.48 EndZ=0
    g3: LineSegment StartX=31.25 StartY=41.48 StartZ=0 EndX=31.25 EndY=58.09 EndZ=0
  constraints (12):
    c: Coincident(g0,g1)
    c: Coincident(g1,g2)
    c: Coincident(g2,g3)
    c: Coincident(g3,g0)
    c: Horizontal(g0)
    c: Horizontal(g2)
    c: Vertical(g1)
    c: Vertical(g3)
    c: DistanceX(g-1,g2) = 31.25
    c: DistanceX(g-1,g1) = 46.41
    c: DistanceY(g-1,g2) = 41.48
    c: DistanceY(g-1,g0) = 58.09
FEATURE [Sketcher::SketchObject] Sketch039  label="IMU"
  MapMode = 5
  Placement = pos=(0,0,1.2) rot=(0,0,1;0rad)
  Support = -> [Pocket018]
  sketch-geometry (4):
    g0: LineSegment StartX=11.27 StartY=57.76 StartZ=0 EndX=28.28 EndY=57.76 EndZ=0
    g1: LineSegment StartX=28.28 StartY=57.76 StartZ=0 EndX=28.28 EndY=35.8 EndZ=0
    g2: LineSegment StartX=28.28 StartY=35.8 StartZ=0 EndX=11.27 EndY=35.8 EndZ=0
    g3: LineSegment StartX=11.27 StartY=35.8 StartZ=0 EndX=11.27 EndY=57.76 EndZ=0
  constraints (12):
    c: Coincident(g0,g1)
    c: Coincident(g1,g2)
    c: Coincident(g2,g3)
    c: Coincident(g3,g0)
    c: Horizontal(g0)
    c: Horizontal(g2)
    c: Vertical(g1)
    c: Vertical(g3)
    c: DistanceX(g-1,g2) = 11.27
    c: DistanceX(g-1,g1) = 28.28
    c: DistanceY(g-1,g2) = 35.8
    c: DistanceY(g-1,g0) = 57.76
FEATURE [PartDesign::Pad] Pad012
  BaseFeature = -> Pocket018
  Length = 5
  Length2 = 100
  Profile = -> Sketch036
  Type = 0
FEATURE [PartDesign::Pad] Pad013
  BaseFeature = -> Pad012
  Length = 7.2
  Length2 = 100
  Profile = -> Sketch037
  Type = 0
FEATURE [PartDesign::Pad] Pad014
  BaseFeature = -> Pad013
  Length = 5
  Length2 = 100
  Profile = -> Sketch039
  Type = 0
FEATURE [PartDesign::Pad] Pad015
  BaseFeature = -> Pad014
  Length = 2
  Length2 = 100
  Profile = -> Sketch038
  Type = 0
FEATURE [Sketcher::SketchObject] Sketch040  label="USB"
  MapMode = 5
  Placement = pos=(0,0,1.2) rot=(0,0,1;0rad)
  Support = -> [Pad015]
  sketch-geometry (4):
    g0: LineSegment StartX=-0.6 StartY=31.78 StartZ=0 EndX=3.89 EndY=31.78 EndZ=0
    g1: LineSegment StartX=3.89 StartY=31.78 StartZ=0 EndX=3.89 EndY=24.27 EndZ=0
    g2: LineSegment StartX=3.89 StartY=24.27 StartZ=0 EndX=-0.6 EndY=24.27 EndZ=0
    g3: LineSegment StartX=-0.6 StartY=24.27 StartZ=0 EndX=-0.6 EndY=31.78 EndZ=0
  constraints (12):
    c: Coincident(g0,g1)
    c: Coincident(g1,g2)
    c: Coincident(g2,g3)
    c: Coincident(g3,g0)
    c: Horizontal(g0)
    c: Horizontal(g2)
    c: Vertical(g1)
    c: Vertical(g3)
    c: DistanceX(g2,g-1) = 0.6
    c: DistanceX(g-1,g1) = 3.89
    c: DistanceY(g-1,g2) = 24.27
    c: DistanceY(g-1,g0) = 31.78
FEATURE [PartDesign::Pad] Pad016
  BaseFeature = -> Pad015
  Length = 4
  Length2 = 100
  Profile = -> Sketch040
  Type = 0
FEATURE [PartDesign::Body] Body004  label="PCBBlock"
  Group = -> [ShapeBinder003,Sketch033,Pad011,Sketch034,Pocket017,Sketch035,Pocket018,Sketch036,Sketch037,Sketch038,Sketch039,Pad012,Pad013,Pad014,Pad015,Sketch040,Pad016]
  Origin = -> Origin004
  Placement = pos=(0,0,4) rot=(0,0,1;0rad)
  Tip = -> Pad016
FEATURE [Sketcher::SketchObject] Sketch041  label="FastenHole"
  ExternalGeometry = -> [Sketch031]
  MapMode = 5
  Placement = pos=(-3.5,0,0) rot=(0.57735,-0.57735,-0.57735;2.0944rad)
  Support = -> [Fillet016]
  sketch-geometry (2):
    g0: Circle CenterX=-3 CenterY=7 CenterZ=0 NormalX=0 NormalY=0 NormalZ=1 AngleXU=0 Radius=1.2
    g1: Circle CenterX=-3 CenterY=12 CenterZ=0 NormalX=0 NormalY=0 NormalZ=1 AngleXU=0 Radius=1.2
  constraints (5):
    c: Coincident(g0,g-3)
    c: Vertical(g0,g1)
    c: Radius(g0) = 1.2
    c: Equal(g0,g1)
    c: DistanceY(g0,g1) = 5
FEATURE [PartDesign::Pocket] Pocket019  label="FastenHolePocket"
  BaseFeature = -> Fillet016
  Length = 3
  Length2 = 100
  Profile = -> Sketch041
  Type = 0
FEATURE [PartDesign::Body] Body001  label="BodyBlock"
  Group = -> [ShapeBinder,Sketch001,Pad,DatumPlane,Sketch002,Pocket,DatumPlane001,Sketch003,Pad001,DatumPlane002,Sketch004,Pad002,DatumPlane003,DatumPlane004,DatumPlane005,Sketch005,Pocket001,Sketch006,Pocket002,Sketch007,Pocket003,DatumPlane006,DatumPlane007,Sketch008,Pocket004,Sketch009,Pocket005,Sketch010,Pocket006,Sketch011,Pocket007,Sketch024,Pocket010,Sketch025,Pocket011,Sketch028,Pocket012,Fillet001,+12 more]
  Origin = -> Origin001
  Tip = -> Pocket019
FEATURE [Sketcher::SketchObject] Sketch043  label="ButtonBase001"
  MapMode = 5
  Placement = pos=(0,0,0) rot=(1,0,0;1.5708rad)
  Support = -> [XZ_Plane001]
  sketch-geometry (1):
    g0: Circle CenterX=28.8 CenterY=9.2 CenterZ=0 NormalX=0 NormalY=0 NormalZ=1 AngleXU=0 Radius=3.8
  constraints (1):
    c: Radius(g0) = 3.8
FEATURE [PartDesign::Pad] Pad017  label="ButtonBasePad001"
  Length = 1.4
  Length2 = 100
  Placement = pos=(0,0,0) rot=(1,0,0;1.5708rad)
  Profile = -> Sketch043
  Type = 0
FEATURE [Sketcher::SketchObject] Sketch044  label="ButtonBody001"
  ExternalGeometry = -> [Pad017]
  MapMode = 5
  Placement = pos=(0,-1.4,0) rot=(1,0,0;1.5708rad)
  Support = -> [Pad017]
  sketch-geometry (1):
    g0: Circle CenterX=28.8 CenterY=9.2 CenterZ=0 NormalX=0 NormalY=0 NormalZ=1 AngleXU=0 Radius=3.2
  constraints (2):
    c: Coincident(g0,g-3)
    c: Radius(g0) = 3.2
FEATURE [PartDesign::Pad] Pad018  label="ButtonBodyPad001"
  BaseFeature = -> Pad017
  Length = 2.4
  Length2 = 100
  Placement = pos=(0,0,0) rot=(1,0,0;1.5708rad)
  Profile = -> Sketch044
  Type = 0
FEATURE [PartDesign::Fillet] Fillet017  label="FilletButtonEdge001"
  Base = -> Pad018 [Edge6]
  BaseFeature = -> Pad018
  Placement = pos=(0,0,0) rot=(1,0,0;1.5708rad)
  Radius = 1
FEATURE [PartDesign::Body] Body005  label="SlimButton-NoPocket"
  Group = -> [Sketch043,Pad017,Sketch044,Pad018,Fillet017]
  Origin = -> Origin005
  Placement = pos=(49,0.6,0) rot=(0,0,1;0rad)
  Tip = -> Fillet017
FEATURE [Sketcher::SketchObject] Sketch045
  MapMode = 5
  Placement = pos=(0,0,0) rot=(1,0,0;1.5708rad)
  Support = -> [XZ_Plane007]
  sketch-geometry (1):
    g0: Circle CenterX=28.8 CenterY=9.2 CenterZ=0 NormalX=0 NormalY=0 NormalZ=1 AngleXU=0 Radius=3
  constraints (3):
    c: Radius(g0) = 3
    c: DistanceX(g-1,g0) = 28.8
    c: DistanceY(g-1,g0) = 9.2
FEATURE [PartDesign::Pad] Pad019
  Length = 1.5
  Length2 = 100
  Placement = pos=(0,0,0) rot=(1,0,0;1.5708rad)
  Profile = -> Sketch045
  Reversed = true
  Type = 0
FEATURE [Sketcher::SketchObject] Sketch046
  MapMode = 5
  Placement = pos=(0,0,0) rot=(1,0,0;1.5708rad)
  Support = -> [XZ_Plane006]
  sketch-geometry (1):
    g0: Circle CenterX=28.8 CenterY=9.2 CenterZ=0 NormalX=0 NormalY=0 NormalZ=1 AngleXU=0 Radius=3.8
  constraints (3):
    c: DistanceX(g-1,g0) = 28.8
    c: DistanceY(g-1,g0) = 9.2
    c: Radius(g0) = 3.8
FEATURE [PartDesign::Pad] Pad020
  Length = 1.4
  Length2 = 100
  Placement = pos=(0,0,0) rot=(1,0,0;1.5708rad)
  Profile = -> Sketch046
  Type = 0
FEATURE [Sketcher::SketchObject] Sketch047
  ExternalGeometry = -> [Pad020]
  MapMode = 5
  Placement = pos=(0,-1.4,0) rot=(1,0,0;1.5708rad)
  Support = -> [Pad020]
  sketch-geometry (1):
    g0: Circle CenterX=28.8 CenterY=9.2 CenterZ=0 NormalX=0 NormalY=0 NormalZ=1 AngleXU=0 Radius=3.2
  constraints (2):
    c: Coincident(g0,g-3)
    c: Radius(g0) = 3.2
FEATURE [PartDesign::Pad] Pad021
  BaseFeature = -> Pad020
  Length = 2.4
  Length2 = 100
  Placement = pos=(0,0,0) rot=(1,0,0;1.5708rad)
  Profile = -> Sketch047
  Type = 0
FEATURE [Sketcher::SketchObject] Sketch048
  ExternalGeometry = -> [Pad019]
  MapMode = 5
  Placement = pos=(0,0,0) rot=(1,0,0;1.5708rad)
  Support = -> [Pad019]
  sketch-geometry (1):
    g0: Circle CenterX=28.8 CenterY=9.2 CenterZ=0 NormalX=0 NormalY=0 NormalZ=1 AngleXU=0 Radius=1.7
  constraints (2):
    c: Coincident(g0,g-3)
    c: Radius(g0) = 1.7
FEATURE [PartDesign::Pad] Pad022
  BaseFeature = -> Pad019
  Length = 0.8
  Length2 = 100
  Placement = pos=(0,0,0) rot=(1,0,0;1.5708rad)
  Profile = -> Sketch048
  Type = 0
FEATURE [PartDesign::Body] Body007  label="ButtonPod"
  Group = -> [Sketch045,Pad019,Sketch048,Pad022]
  Origin = -> Origin007
  Tip = -> Pad022
FEATURE [Sketcher::SketchObject] Sketch049
  ExternalGeometry = -> [Pad021]
  MapMode = 5
  Placement = pos=(0,0,0) rot=(-1,0,0;1.5708rad)
  Support = -> [Pad021]
  sketch-geometry (1):
    g0: Circle CenterX=28.8 CenterY=-9.2 CenterZ=0 NormalX=0 NormalY=0 NormalZ=1 AngleXU=0 Radius=2
  constraints (2):
    c: Coincident(g0,g-3)
    c: Radius(g0) = 2
FEATURE [PartDesign::Pocket] Pocket020
  BaseFeature = -> Pad021
  Length = 1
  Length2 = 100
  Placement = pos=(0,0,0) rot=(1,0,0;1.5708rad)
  Profile = -> Sketch049
  Type = 0
FEATURE [PartDesign::Fillet] Fillet018
  Base = -> Pocket020 [Edge9]
  BaseFeature = -> Pocket020
  Placement = pos=(0,0,0) rot=(1,0,0;1.5708rad)
  Radius = 1
FEATURE [PartDesign::Body] Body006  label="SlimButton"
  Group = -> [Sketch046,Pad020,Sketch047,Pad021,Sketch049,Pocket020,Fillet018]
  Origin = -> Origin006
  Tip = -> Fillet018
FEATURE [Sketcher::SketchObject] Sketch050  label="IMUOutline"
  MapMode = 5
  Support = -> [XY_Plane008]
  sketch-geometry (4):
    g0: LineSegment StartX=0 StartY=-20 StartZ=0 EndX=17 EndY=-20 EndZ=0
    g1: LineSegment StartX=17 StartY=-20 StartZ=0 EndX=17 EndY=-42 EndZ=0
    g2: LineSegment StartX=17 StartY=-42 StartZ=0 EndX=0 EndY=-42 EndZ=0
    g3: LineSegment StartX=0 StartY=-42 StartZ=0 EndX=0 EndY=-20 EndZ=0
  constraints (12):
    c: Coincident(g0,g1)
    c: Coincident(g1,g2)
    c: Coincident(g2,g3)
    c: Coincident(g3,g0)
    c: Horizontal(g0)
    c: Horizontal(g2)
    c: Vertical(g1)
    c: Vertical(g3)
    c: PointOnObject(g0,g-2)
    c: DistanceX(g0,g0) = 17
    c: DistanceY(g1,g1) = 22
    c: DistanceY(g0,g-1) = 20
FEATURE [Sketcher::SketchObject] Sketch051  label="CoverOuterline"
  ExternalGeometry = -> [Sketch050]
  MapMode = 5
  Support = -> [XY_Plane008]
  sketch-geometry (4):
    g0: LineSegment StartX=-0.8 StartY=-19 StartZ=0 EndX=18 EndY=-19 EndZ=0
    g1: LineSegment StartX=18 StartY=-19 StartZ=0 EndX=18 EndY=-43 EndZ=0
    g2: LineSegment StartX=18 StartY=-43 StartZ=0 EndX=-0.8 EndY=-43 EndZ=0
    g3: LineSegment StartX=-0.8 StartY=-43 StartZ=0 EndX=-0.8 EndY=-19 EndZ=0
  constraints (12):
    c: Coincident(g0,g1)
    c: Coincident(g1,g2)
    c: Coincident(g2,g3)
    c: Coincident(g3,g0)
    c: Horizontal(g0)
    c: Horizontal(g2)
    c: Vertical(g1)
    c: Vertical(g3)
    c: DistanceX(g0,g-3) = 0.8
    c: DistanceY(g-3,g0) = 1
    c: DistanceX(g-4,g1) = 1
    c: DistanceY(g2,g-4) = 1
FEATURE [PartDesign::Pad] Pad023
  Length = 5
  Length2 = 100
  Profile = -> Sketch051
  Type = 0
FEATURE [Sketcher::SketchObject] Sketch052
  ExternalGeometry = -> [Sketch050]
  MapMode = 5
  Placement = pos=(0,0,5) rot=(0,0,1;0rad)
  Support = -> [Pad023]
  sketch-geometry (4):
    g0: LineSegment StartX=0 StartY=-20 StartZ=0 EndX=17 EndY=-20 EndZ=0
    g1: LineSegment StartX=17 StartY=-20 StartZ=0 EndX=17 EndY=-42 EndZ=0
    g2: LineSegment StartX=17 StartY=-42 StartZ=0 EndX=0 EndY=-42 EndZ=0
    g3: LineSegment StartX=0 StartY=-42 StartZ=0 EndX=0 EndY=-20 EndZ=0
  constraints (10):
    c: Coincident(g0,g1)
    c: Coincident(g1,g2)
    c: Coincident(g2,g3)
    c: Coincident(g3,g0)
    c: Horizontal(g0)
    c: Horizontal(g2)
    c: Vertical(g1)
    c: Vertical(g3)
    c: Coincident(g0,g-3)
    c: Coincident(g-4,g1)
FEATURE [PartDesign::Pocket] Pocket021
  BaseFeature = -> Pad023
  Length = 4.2
  Length2 = 100
  Profile = -> Sketch052
  Type = 0
FEATURE [PartDesign::Body] Body008  label="IMUCover"
  Group = -> [Sketch050,Sketch051,Pad023,Sketch052,Pocket021]
  Origin = -> Origin008
  Tip = -> Pocket021
FEATURE [Mesh::Feature] Mesh003  label="IMUCoverMesh"
FEATURE [Mesh::Feature] Mesh  label="SlimButtonMesh-NoPocket"
FEATURE [Mesh::Feature] Mesh004  label="SlimButtonMesh"
FEATURE [Mesh::Feature] Mesh005  label="SlimButton-Spacer"
FEATURE [Mesh::Feature] Mesh006  label="CoverMeash"
